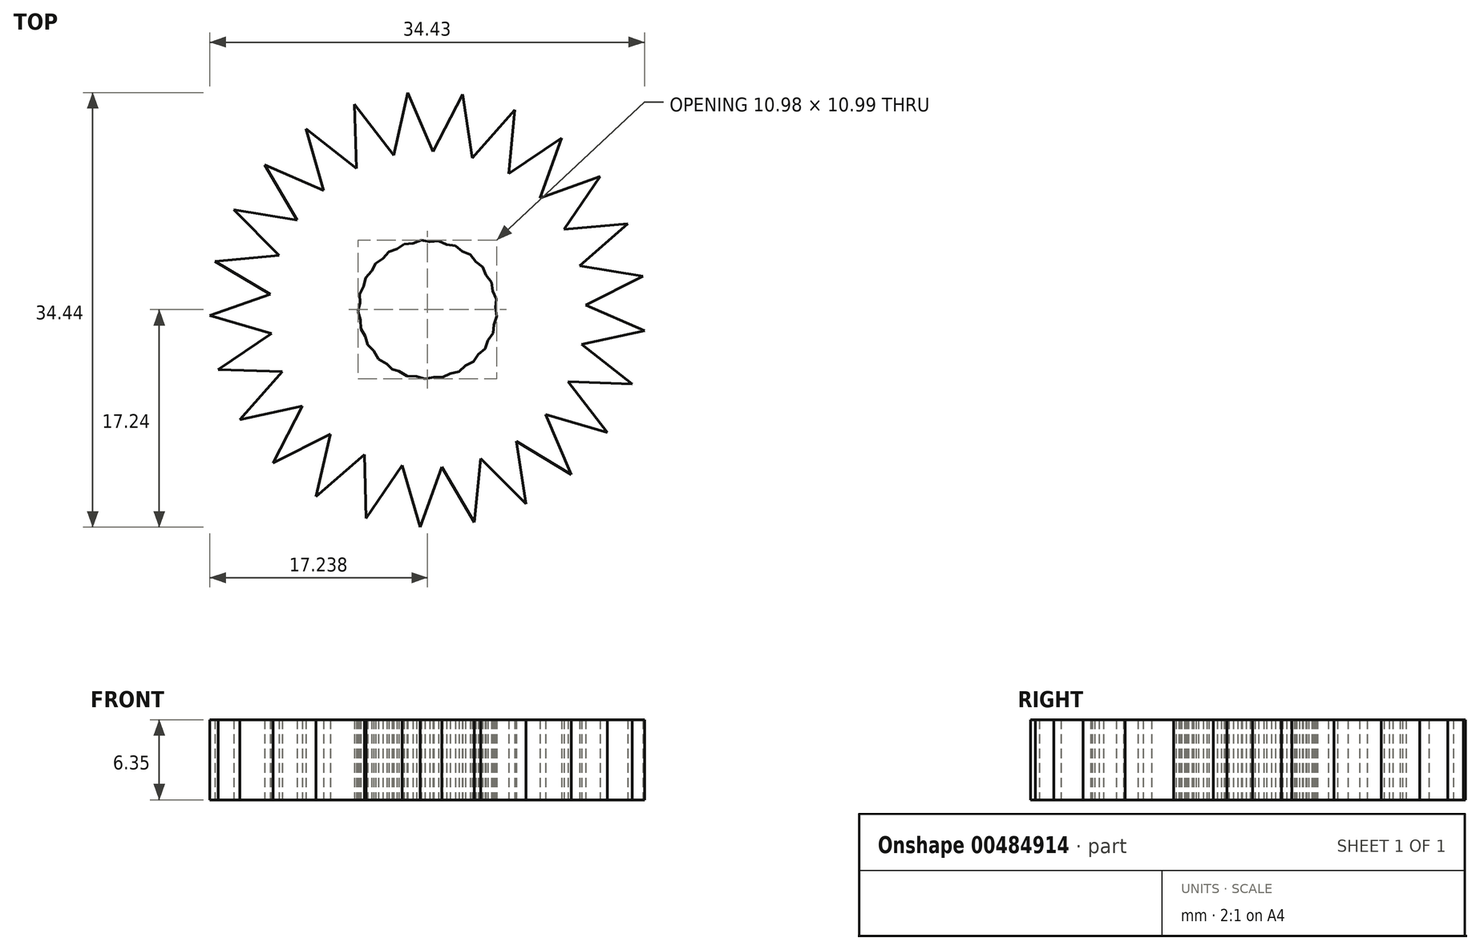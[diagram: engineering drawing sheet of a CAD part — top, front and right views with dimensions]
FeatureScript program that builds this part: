
annotation { "Feature Type Name" : "Feature", "Feature Type Description" : "" }
export const myFeature = defineFeature(function(context is Context, id is Id, definition is map)
    precondition{}
    {
        {
            var Q0;
            Q0=qCreatedBy(makeId("Top.planeOp"),FACE);
            var sketch = newSketch(context, id + "F0", { "sketchPlane" : qUnion([Q0])});
            skLineSegment(sketch, "E0", {"start": v(-12.25, -12.16) * mm, "end": v(2.76, 17.04) * mm});
            skLineSegment(sketch, "E1", {"start": v(2.76, 17.04) * mm, "end": v(7.78, -15.4) * mm});
            skLineSegment(sketch, "E2", {"start": v(7.78, -15.4) * mm, "end": v(-15.35, 7.9) * mm});
            skLineSegment(sketch, "E3", {"start": v(-15.35, 7.9) * mm, "end": v(17.06, 2.64) * mm});
            skLineSegment(sketch, "E4", {"start": v(17.06, 2.64) * mm, "end": v(-12.25, -12.16) * mm});
            skLineSegment(sketch, "E5", {"start": v(-14.89, -8.73) * mm, "end": v(6.91, 15.82) * mm});
            skLineSegment(sketch, "E6", {"start": v(6.91, 15.82) * mm, "end": v(3.7, -16.86) * mm});
            skLineSegment(sketch, "E7", {"start": v(3.7, -16.86) * mm, "end": v(-12.9, 11.46) * mm});
            skLineSegment(sketch, "E8", {"start": v(-12.9, 11.46) * mm, "end": v(17.18, -1.69) * mm});
            skLineSegment(sketch, "E9", {"start": v(17.18, -1.69) * mm, "end": v(-14.89, -8.73) * mm});
            skLineSegment(sketch, "E10", {"start": v(-16.6, -4.76) * mm, "end": v(10.63, 13.6) * mm});
            skLineSegment(sketch, "E11", {"start": v(10.63, 13.6) * mm, "end": v(-0.6, -17.25) * mm});
            skLineSegment(sketch, "E12", {"start": v(-0.6, -17.25) * mm, "end": v(-9.65, 14.3) * mm});
            skLineSegment(sketch, "E13", {"start": v(-9.65, 14.3) * mm, "end": v(16.22, -5.9) * mm});
            skLineSegment(sketch, "E14", {"start": v(16.22, -5.9) * mm, "end": v(-16.6, -4.76) * mm});
            skLineSegment(sketch, "E15", {"start": v(-17.25, -0.48) * mm, "end": v(13.68, 10.53) * mm});
            skLineSegment(sketch, "E16", {"start": v(-4.87, -16.56) * mm, "end": v(-5.79, 16.26) * mm});
            skLineSegment(sketch, "E17", {"start": v(-5.79, 16.26) * mm, "end": v(14.24, -9.75) * mm});
            skLineSegment(sketch, "E18", {"start": v(14.24, -9.75) * mm, "end": v(-17.25, -0.48) * mm});
            skLineSegment(sketch, "E19", {"start": v(-16.83, 3.82) * mm, "end": v(15.86, 6.8) * mm});
            skLineSegment(sketch, "E20", {"start": v(15.86, 6.8) * mm, "end": v(-8.84, -14.82) * mm});
            skLineSegment(sketch, "E21", {"start": v(-8.84, -14.82) * mm, "end": v(-1.56, 17.19) * mm});
            skLineSegment(sketch, "E22", {"start": v(11.4, -13.08) * mm, "end": v(-16.83, 3.82) * mm});
            skLineSegment(sketch, "E23", {"start": v(13.68, 10.53) * mm, "end": v(-4.87, -16.56) * mm});
            skLineSegment(sketch, "E24", {"start": v(-1.56, 17.19) * mm, "end": v(11.4, -13.08) * mm});
            skSolve(sketch);
        }
        {
            var Q0;
            {var subQ0=sQuery(id+"F0.wireOp",EDGE,"E4");var subQ1=sQuery(id+"F0.wireOp",EDGE,"E0");var subQ2=makeQuery(id+"F0.imprint","INTERSECT",VERTEX,{"derivedFrom":[subQ1,subQ0]});Q0=makeQuery(id+"F0.imprint","IMPRINT",FACE,{"disambiguationData":[TD([[makeQuery(id+"F0.imprint","IMPRINT",EDGE,{"disambiguationData":[TD([[subQ2,-1.0]])],"derivedFrom":subQ1}),-1.0]])]});}
            var Q1;
            {var subQ0=sQuery(id+"F0.wireOp",EDGE,"E9");var subQ1=sQuery(id+"F0.wireOp",EDGE,"E0");var subQ2=makeQuery(id+"F0.imprint","INTERSECT",VERTEX,{"derivedFrom":[subQ1,subQ0]});Q1=makeQuery(id+"F0.imprint","IMPRINT",FACE,{"disambiguationData":[TD([[makeQuery(id+"F0.imprint","IMPRINT",EDGE,{"disambiguationData":[TD([[subQ2,-1.0]])],"derivedFrom":subQ1}),1.0]])]});}
            var Q2;
            {var subQ0=sQuery(id+"F0.wireOp",EDGE,"E24");var subQ1=sQuery(id+"F0.wireOp",EDGE,"E0");var subQ2=makeQuery(id+"F0.imprint","INTERSECT",VERTEX,{"derivedFrom":[subQ1,subQ0]});Q2=makeQuery(id+"F0.imprint","IMPRINT",FACE,{"disambiguationData":[TD([[makeQuery(id+"F0.imprint","IMPRINT",EDGE,{"disambiguationData":[TD([[subQ2,1.0]])],"derivedFrom":subQ1}),1.0]])]});}
            var Q3;
            {var subQ0=sQuery(id+"F0.wireOp",EDGE,"E1");var subQ1=sQuery(id+"F0.wireOp",EDGE,"E0");var subQ2=makeQuery(id+"F0.imprint","INTERSECT",VERTEX,{"derivedFrom":[subQ1,subQ0]});Q3=makeQuery(id+"F0.imprint","IMPRINT",FACE,{"disambiguationData":[TD([[makeQuery(id+"F0.imprint","IMPRINT",EDGE,{"disambiguationData":[TD([[subQ2,1.0]])],"derivedFrom":subQ1}),-1.0]])]});}
            var Q4;
            {var subQ0=sQuery(id+"F0.wireOp",EDGE,"E5");var subQ1=sQuery(id+"F0.wireOp",EDGE,"E1");var subQ2=makeQuery(id+"F0.imprint","INTERSECT",VERTEX,{"derivedFrom":[subQ1,subQ0]});Q4=makeQuery(id+"F0.imprint","IMPRINT",FACE,{"disambiguationData":[TD([[makeQuery(id+"F0.imprint","IMPRINT",EDGE,{"disambiguationData":[TD([[subQ2,-1.0]])],"derivedFrom":subQ1}),1.0]])]});}
            var Q5;
            {var subQ0=sQuery(id+"F0.wireOp",EDGE,"E22");var subQ1=sQuery(id+"F0.wireOp",EDGE,"E1");var subQ2=makeQuery(id+"F0.imprint","INTERSECT",VERTEX,{"derivedFrom":[subQ1,subQ0]});Q5=makeQuery(id+"F0.imprint","IMPRINT",FACE,{"disambiguationData":[TD([[makeQuery(id+"F0.imprint","IMPRINT",EDGE,{"disambiguationData":[TD([[subQ2,1.0]])],"derivedFrom":subQ1}),1.0]])]});}
            var Q6;
            {var subQ0=sQuery(id+"F0.wireOp",EDGE,"E2");var subQ1=sQuery(id+"F0.wireOp",EDGE,"E1");var subQ2=makeQuery(id+"F0.imprint","INTERSECT",VERTEX,{"derivedFrom":[subQ1,subQ0]});Q6=makeQuery(id+"F0.imprint","IMPRINT",FACE,{"disambiguationData":[TD([[makeQuery(id+"F0.imprint","IMPRINT",EDGE,{"disambiguationData":[TD([[subQ2,1.0]])],"derivedFrom":subQ1}),-1.0]])]});}
            var Q7;
            {var subQ0=sQuery(id+"F0.wireOp",EDGE,"E6");var subQ1=sQuery(id+"F0.wireOp",EDGE,"E2");var subQ2=makeQuery(id+"F0.imprint","INTERSECT",VERTEX,{"derivedFrom":[subQ1,subQ0]});Q7=makeQuery(id+"F0.imprint","IMPRINT",FACE,{"disambiguationData":[TD([[makeQuery(id+"F0.imprint","IMPRINT",EDGE,{"disambiguationData":[TD([[subQ2,-1.0]])],"derivedFrom":subQ1}),1.0]])]});}
            var Q8;
            {var subQ0=sQuery(id+"F0.wireOp",EDGE,"E19");var subQ1=sQuery(id+"F0.wireOp",EDGE,"E2");var subQ2=makeQuery(id+"F0.imprint","INTERSECT",VERTEX,{"derivedFrom":[subQ1,subQ0]});Q8=makeQuery(id+"F0.imprint","IMPRINT",FACE,{"disambiguationData":[TD([[makeQuery(id+"F0.imprint","IMPRINT",EDGE,{"disambiguationData":[TD([[subQ2,1.0]])],"derivedFrom":subQ1}),1.0]])]});}
            var Q9;
            {var subQ0=sQuery(id+"F0.wireOp",EDGE,"E3");var subQ1=sQuery(id+"F0.wireOp",EDGE,"E2");var subQ2=makeQuery(id+"F0.imprint","INTERSECT",VERTEX,{"derivedFrom":[subQ1,subQ0]});Q9=makeQuery(id+"F0.imprint","IMPRINT",FACE,{"disambiguationData":[TD([[makeQuery(id+"F0.imprint","IMPRINT",EDGE,{"disambiguationData":[TD([[subQ2,1.0]])],"derivedFrom":subQ1}),-1.0]])]});}
            var Q10;
            {var subQ0=sQuery(id+"F0.wireOp",EDGE,"E7");var subQ1=sQuery(id+"F0.wireOp",EDGE,"E3");var subQ2=makeQuery(id+"F0.imprint","INTERSECT",VERTEX,{"derivedFrom":[subQ1,subQ0]});Q10=makeQuery(id+"F0.imprint","IMPRINT",FACE,{"disambiguationData":[TD([[makeQuery(id+"F0.imprint","IMPRINT",EDGE,{"disambiguationData":[TD([[subQ2,-1.0]])],"derivedFrom":subQ1}),1.0]])]});}
            var Q11;
            {var subQ0=sQuery(id+"F0.wireOp",EDGE,"E20");var subQ1=sQuery(id+"F0.wireOp",EDGE,"E3");var subQ2=makeQuery(id+"F0.imprint","INTERSECT",VERTEX,{"derivedFrom":[subQ1,subQ0]});Q11=makeQuery(id+"F0.imprint","IMPRINT",FACE,{"disambiguationData":[TD([[makeQuery(id+"F0.imprint","IMPRINT",EDGE,{"disambiguationData":[TD([[subQ2,1.0]])],"derivedFrom":subQ1}),1.0]])]});}
            var Q12;
            {var subQ0=sQuery(id+"F0.wireOp",EDGE,"E4");var subQ1=sQuery(id+"F0.wireOp",EDGE,"E3");var subQ2=makeQuery(id+"F0.imprint","INTERSECT",VERTEX,{"derivedFrom":[subQ1,subQ0]});Q12=makeQuery(id+"F0.imprint","IMPRINT",FACE,{"disambiguationData":[TD([[makeQuery(id+"F0.imprint","IMPRINT",EDGE,{"disambiguationData":[TD([[subQ2,1.0]])],"derivedFrom":subQ1}),-1.0]])]});}
            var Q13;
            {var subQ0=sQuery(id+"F0.wireOp",EDGE,"E8");var subQ1=sQuery(id+"F0.wireOp",EDGE,"E4");var subQ2=makeQuery(id+"F0.imprint","INTERSECT",VERTEX,{"derivedFrom":[subQ1,subQ0]});Q13=makeQuery(id+"F0.imprint","IMPRINT",FACE,{"disambiguationData":[TD([[makeQuery(id+"F0.imprint","IMPRINT",EDGE,{"disambiguationData":[TD([[subQ2,-1.0]])],"derivedFrom":subQ1}),1.0]])]});}
            var Q14;
            {var subQ0=sQuery(id+"F0.wireOp",EDGE,"E21");var subQ1=sQuery(id+"F0.wireOp",EDGE,"E4");var subQ2=makeQuery(id+"F0.imprint","INTERSECT",VERTEX,{"derivedFrom":[subQ1,subQ0]});Q14=makeQuery(id+"F0.imprint","IMPRINT",FACE,{"disambiguationData":[TD([[makeQuery(id+"F0.imprint","IMPRINT",EDGE,{"disambiguationData":[TD([[subQ2,1.0]])],"derivedFrom":subQ1}),1.0]])]});}
            var Q15;
            {var subQ0=sQuery(id+"F0.wireOp",EDGE,"E14");var subQ1=sQuery(id+"F0.wireOp",EDGE,"E5");var subQ2=makeQuery(id+"F0.imprint","INTERSECT",VERTEX,{"derivedFrom":[subQ1,subQ0]});Q15=makeQuery(id+"F0.imprint","IMPRINT",FACE,{"disambiguationData":[TD([[makeQuery(id+"F0.imprint","IMPRINT",EDGE,{"disambiguationData":[TD([[subQ2,-1.0]])],"derivedFrom":subQ1}),1.0]])]});}
            var Q16;
            {var subQ0=sQuery(id+"F0.wireOp",EDGE,"E10");var subQ1=sQuery(id+"F0.wireOp",EDGE,"E6");var subQ2=makeQuery(id+"F0.imprint","INTERSECT",VERTEX,{"derivedFrom":[subQ1,subQ0]});Q16=makeQuery(id+"F0.imprint","IMPRINT",FACE,{"disambiguationData":[TD([[makeQuery(id+"F0.imprint","IMPRINT",EDGE,{"disambiguationData":[TD([[subQ2,-1.0]])],"derivedFrom":subQ1}),1.0]])]});}
            var Q17;
            {var subQ0=sQuery(id+"F0.wireOp",EDGE,"E11");var subQ1=sQuery(id+"F0.wireOp",EDGE,"E7");var subQ2=makeQuery(id+"F0.imprint","INTERSECT",VERTEX,{"derivedFrom":[subQ1,subQ0]});Q17=makeQuery(id+"F0.imprint","IMPRINT",FACE,{"disambiguationData":[TD([[makeQuery(id+"F0.imprint","IMPRINT",EDGE,{"disambiguationData":[TD([[subQ2,-1.0]])],"derivedFrom":subQ1}),1.0]])]});}
            var Q18;
            {var subQ0=sQuery(id+"F0.wireOp",EDGE,"E12");var subQ1=sQuery(id+"F0.wireOp",EDGE,"E8");var subQ2=makeQuery(id+"F0.imprint","INTERSECT",VERTEX,{"derivedFrom":[subQ1,subQ0]});Q18=makeQuery(id+"F0.imprint","IMPRINT",FACE,{"disambiguationData":[TD([[makeQuery(id+"F0.imprint","IMPRINT",EDGE,{"disambiguationData":[TD([[subQ2,-1.0]])],"derivedFrom":subQ1}),1.0]])]});}
            var Q19;
            {var subQ0=sQuery(id+"F0.wireOp",EDGE,"E13");var subQ1=sQuery(id+"F0.wireOp",EDGE,"E9");var subQ2=makeQuery(id+"F0.imprint","INTERSECT",VERTEX,{"derivedFrom":[subQ1,subQ0]});Q19=makeQuery(id+"F0.imprint","IMPRINT",FACE,{"disambiguationData":[TD([[makeQuery(id+"F0.imprint","IMPRINT",EDGE,{"disambiguationData":[TD([[subQ2,-1.0]])],"derivedFrom":subQ1}),1.0]])]});}
            var Q20;
            {var subQ0=sQuery(id+"F0.wireOp",EDGE,"E18");var subQ1=sQuery(id+"F0.wireOp",EDGE,"E10");var subQ2=makeQuery(id+"F0.imprint","INTERSECT",VERTEX,{"derivedFrom":[subQ1,subQ0]});Q20=makeQuery(id+"F0.imprint","IMPRINT",FACE,{"disambiguationData":[TD([[makeQuery(id+"F0.imprint","IMPRINT",EDGE,{"disambiguationData":[TD([[subQ2,-1.0]])],"derivedFrom":subQ1}),1.0]])]});}
            var Q21;
            {var subQ0=sQuery(id+"F0.wireOp",EDGE,"E15");var subQ1=sQuery(id+"F0.wireOp",EDGE,"E11");var subQ2=makeQuery(id+"F0.imprint","INTERSECT",VERTEX,{"derivedFrom":[subQ1,subQ0]});Q21=makeQuery(id+"F0.imprint","IMPRINT",FACE,{"disambiguationData":[TD([[makeQuery(id+"F0.imprint","IMPRINT",EDGE,{"disambiguationData":[TD([[subQ2,-1.0]])],"derivedFrom":subQ1}),1.0]])]});}
            var Q22;
            {var subQ0=sQuery(id+"F0.wireOp",EDGE,"E23");var subQ1=sQuery(id+"F0.wireOp",EDGE,"E12");var subQ2=makeQuery(id+"F0.imprint","INTERSECT",VERTEX,{"derivedFrom":[subQ1,subQ0]});Q22=makeQuery(id+"F0.imprint","IMPRINT",FACE,{"disambiguationData":[TD([[makeQuery(id+"F0.imprint","IMPRINT",EDGE,{"disambiguationData":[TD([[subQ2,-1.0]])],"derivedFrom":subQ1}),1.0]])]});}
            var Q23;
            {var subQ0=sQuery(id+"F0.wireOp",EDGE,"E16");var subQ1=sQuery(id+"F0.wireOp",EDGE,"E13");var subQ2=makeQuery(id+"F0.imprint","INTERSECT",VERTEX,{"derivedFrom":[subQ1,subQ0]});Q23=makeQuery(id+"F0.imprint","IMPRINT",FACE,{"disambiguationData":[TD([[makeQuery(id+"F0.imprint","IMPRINT",EDGE,{"disambiguationData":[TD([[subQ2,-1.0]])],"derivedFrom":subQ1}),1.0]])]});}
            var Q24;
            {var subQ0=sQuery(id+"F0.wireOp",EDGE,"E17");var subQ1=sQuery(id+"F0.wireOp",EDGE,"E14");var subQ2=makeQuery(id+"F0.imprint","INTERSECT",VERTEX,{"derivedFrom":[subQ1,subQ0]});Q24=makeQuery(id+"F0.imprint","IMPRINT",FACE,{"disambiguationData":[TD([[makeQuery(id+"F0.imprint","IMPRINT",EDGE,{"disambiguationData":[TD([[subQ2,-1.0]])],"derivedFrom":subQ1}),1.0]])]});}
            var Q25;
            {var subQ0=sQuery(id+"F0.wireOp",EDGE,"E14");var subQ1=sQuery(id+"F0.wireOp",EDGE,"E0");var subQ2=makeQuery(id+"F0.imprint","INTERSECT",VERTEX,{"derivedFrom":[subQ1,subQ0]});Q25=makeQuery(id+"F0.imprint","IMPRINT",FACE,{"disambiguationData":[TD([[makeQuery(id+"F0.imprint","IMPRINT",EDGE,{"disambiguationData":[TD([[subQ2,-1.0]])],"derivedFrom":subQ1}),1.0]])]});}
            var Q26;
            {var subQ0=sQuery(id+"F0.wireOp",EDGE,"E24");var subQ1=sQuery(id+"F0.wireOp",EDGE,"E0");var subQ2=makeQuery(id+"F0.imprint","INTERSECT",VERTEX,{"derivedFrom":[subQ1,subQ0]});Q26=makeQuery(id+"F0.imprint","IMPRINT",FACE,{"disambiguationData":[TD([[makeQuery(id+"F0.imprint","IMPRINT",EDGE,{"disambiguationData":[TD([[subQ2,1.0]])],"derivedFrom":subQ1}),-1.0]])]});}
            var Q27;
            {var subQ0=sQuery(id+"F0.wireOp",EDGE,"E10");var subQ1=sQuery(id+"F0.wireOp",EDGE,"E1");var subQ2=makeQuery(id+"F0.imprint","INTERSECT",VERTEX,{"derivedFrom":[subQ1,subQ0]});Q27=makeQuery(id+"F0.imprint","IMPRINT",FACE,{"disambiguationData":[TD([[makeQuery(id+"F0.imprint","IMPRINT",EDGE,{"disambiguationData":[TD([[subQ2,-1.0]])],"derivedFrom":subQ1}),1.0]])]});}
            var Q28;
            {var subQ0=sQuery(id+"F0.wireOp",EDGE,"E14");var subQ1=sQuery(id+"F0.wireOp",EDGE,"E1");var subQ2=makeQuery(id+"F0.imprint","INTERSECT",VERTEX,{"derivedFrom":[subQ1,subQ0]});Q28=makeQuery(id+"F0.imprint","IMPRINT",FACE,{"disambiguationData":[TD([[makeQuery(id+"F0.imprint","IMPRINT",EDGE,{"disambiguationData":[TD([[subQ2,-1.0]])],"derivedFrom":subQ1}),1.0]])]});}
            var Q29;
            {var subQ0=sQuery(id+"F0.wireOp",EDGE,"E6");var subQ1=sQuery(id+"F0.wireOp",EDGE,"E2");var subQ2=makeQuery(id+"F0.imprint","INTERSECT",VERTEX,{"derivedFrom":[subQ1,subQ0]});Q29=makeQuery(id+"F0.imprint","IMPRINT",FACE,{"disambiguationData":[TD([[makeQuery(id+"F0.imprint","IMPRINT",EDGE,{"disambiguationData":[TD([[subQ2,-1.0]])],"derivedFrom":subQ1}),-1.0]])]});}
            var Q30;
            {var subQ0=sQuery(id+"F0.wireOp",EDGE,"E11");var subQ1=sQuery(id+"F0.wireOp",EDGE,"E2");var subQ2=makeQuery(id+"F0.imprint","INTERSECT",VERTEX,{"derivedFrom":[subQ1,subQ0]});Q30=makeQuery(id+"F0.imprint","IMPRINT",FACE,{"disambiguationData":[TD([[makeQuery(id+"F0.imprint","IMPRINT",EDGE,{"disambiguationData":[TD([[subQ2,-1.0]])],"derivedFrom":subQ1}),1.0]])]});}
            var Q31;
            {var subQ0=sQuery(id+"F0.wireOp",EDGE,"E10");var subQ1=sQuery(id+"F0.wireOp",EDGE,"E2");var subQ2=makeQuery(id+"F0.imprint","INTERSECT",VERTEX,{"derivedFrom":[subQ1,subQ0]});Q31=makeQuery(id+"F0.imprint","IMPRINT",FACE,{"disambiguationData":[TD([[makeQuery(id+"F0.imprint","IMPRINT",EDGE,{"disambiguationData":[TD([[subQ2,-1.0]])],"derivedFrom":subQ1}),1.0]])]});}
            var Q32;
            {var subQ0=sQuery(id+"F0.wireOp",EDGE,"E7");var subQ1=sQuery(id+"F0.wireOp",EDGE,"E3");var subQ2=makeQuery(id+"F0.imprint","INTERSECT",VERTEX,{"derivedFrom":[subQ1,subQ0]});Q32=makeQuery(id+"F0.imprint","IMPRINT",FACE,{"disambiguationData":[TD([[makeQuery(id+"F0.imprint","IMPRINT",EDGE,{"disambiguationData":[TD([[subQ2,-1.0]])],"derivedFrom":subQ1}),-1.0]])]});}
            var Q33;
            {var subQ0=sQuery(id+"F0.wireOp",EDGE,"E12");var subQ1=sQuery(id+"F0.wireOp",EDGE,"E3");var subQ2=makeQuery(id+"F0.imprint","INTERSECT",VERTEX,{"derivedFrom":[subQ1,subQ0]});Q33=makeQuery(id+"F0.imprint","IMPRINT",FACE,{"disambiguationData":[TD([[makeQuery(id+"F0.imprint","IMPRINT",EDGE,{"disambiguationData":[TD([[subQ2,-1.0]])],"derivedFrom":subQ1}),1.0]])]});}
            var Q34;
            {var subQ0=sQuery(id+"F0.wireOp",EDGE,"E20");var subQ1=sQuery(id+"F0.wireOp",EDGE,"E3");var subQ2=makeQuery(id+"F0.imprint","INTERSECT",VERTEX,{"derivedFrom":[subQ1,subQ0]});Q34=makeQuery(id+"F0.imprint","IMPRINT",FACE,{"disambiguationData":[TD([[makeQuery(id+"F0.imprint","IMPRINT",EDGE,{"disambiguationData":[TD([[subQ2,1.0]])],"derivedFrom":subQ1}),-1.0]])]});}
            var Q35;
            {var subQ0=sQuery(id+"F0.wireOp",EDGE,"E8");var subQ1=sQuery(id+"F0.wireOp",EDGE,"E4");var subQ2=makeQuery(id+"F0.imprint","INTERSECT",VERTEX,{"derivedFrom":[subQ1,subQ0]});Q35=makeQuery(id+"F0.imprint","IMPRINT",FACE,{"disambiguationData":[TD([[makeQuery(id+"F0.imprint","IMPRINT",EDGE,{"disambiguationData":[TD([[subQ2,-1.0]])],"derivedFrom":subQ1}),-1.0]])]});}
            var Q36;
            {var subQ0=sQuery(id+"F0.wireOp",EDGE,"E12");var subQ1=sQuery(id+"F0.wireOp",EDGE,"E4");var subQ2=makeQuery(id+"F0.imprint","INTERSECT",VERTEX,{"derivedFrom":[subQ1,subQ0]});Q36=makeQuery(id+"F0.imprint","IMPRINT",FACE,{"disambiguationData":[TD([[makeQuery(id+"F0.imprint","IMPRINT",EDGE,{"disambiguationData":[TD([[subQ2,-1.0]])],"derivedFrom":subQ1}),1.0]])]});}
            var Q37;
            {var subQ0=sQuery(id+"F0.wireOp",EDGE,"E21");var subQ1=sQuery(id+"F0.wireOp",EDGE,"E4");var subQ2=makeQuery(id+"F0.imprint","INTERSECT",VERTEX,{"derivedFrom":[subQ1,subQ0]});Q37=makeQuery(id+"F0.imprint","IMPRINT",FACE,{"disambiguationData":[TD([[makeQuery(id+"F0.imprint","IMPRINT",EDGE,{"disambiguationData":[TD([[subQ2,1.0]])],"derivedFrom":subQ1}),-1.0]])]});}
            var Q38;
            {var subQ0=sQuery(id+"F0.wireOp",EDGE,"E18");var subQ1=sQuery(id+"F0.wireOp",EDGE,"E5");var subQ2=makeQuery(id+"F0.imprint","INTERSECT",VERTEX,{"derivedFrom":[subQ1,subQ0]});Q38=makeQuery(id+"F0.imprint","IMPRINT",FACE,{"disambiguationData":[TD([[makeQuery(id+"F0.imprint","IMPRINT",EDGE,{"disambiguationData":[TD([[subQ2,-1.0]])],"derivedFrom":subQ1}),1.0]])]});}
            var Q39;
            {var subQ0=sQuery(id+"F0.wireOp",EDGE,"E15");var subQ1=sQuery(id+"F0.wireOp",EDGE,"E6");var subQ2=makeQuery(id+"F0.imprint","INTERSECT",VERTEX,{"derivedFrom":[subQ1,subQ0]});Q39=makeQuery(id+"F0.imprint","IMPRINT",FACE,{"disambiguationData":[TD([[makeQuery(id+"F0.imprint","IMPRINT",EDGE,{"disambiguationData":[TD([[subQ2,-1.0]])],"derivedFrom":subQ1}),1.0]])]});}
            var Q40;
            {var subQ0=sQuery(id+"F0.wireOp",EDGE,"E17");var subQ1=sQuery(id+"F0.wireOp",EDGE,"E9");var subQ2=makeQuery(id+"F0.imprint","INTERSECT",VERTEX,{"derivedFrom":[subQ1,subQ0]});Q40=makeQuery(id+"F0.imprint","IMPRINT",FACE,{"disambiguationData":[TD([[makeQuery(id+"F0.imprint","IMPRINT",EDGE,{"disambiguationData":[TD([[subQ2,-1.0]])],"derivedFrom":subQ1}),1.0]])]});}
            var Q41;
            {var subQ0=sQuery(id+"F0.wireOp",EDGE,"E7");var subQ1=sQuery(id+"F0.wireOp",EDGE,"E4");var subQ2=makeQuery(id+"F0.imprint","INTERSECT",VERTEX,{"derivedFrom":[subQ1,subQ0]});Q41=makeQuery(id+"F0.imprint","IMPRINT",FACE,{"disambiguationData":[TD([[makeQuery(id+"F0.imprint","IMPRINT",EDGE,{"disambiguationData":[TD([[subQ2,-1.0]])],"derivedFrom":subQ1}),1.0]])]});}
            var Q42;
            {var subQ0=sQuery(id+"F0.wireOp",EDGE,"E16");var subQ1=sQuery(id+"F0.wireOp",EDGE,"E9");var subQ2=makeQuery(id+"F0.imprint","INTERSECT",VERTEX,{"derivedFrom":[subQ1,subQ0]});Q42=makeQuery(id+"F0.imprint","IMPRINT",FACE,{"disambiguationData":[TD([[makeQuery(id+"F0.imprint","IMPRINT",EDGE,{"disambiguationData":[TD([[subQ2,-1.0]])],"derivedFrom":subQ1}),-1.0]])]});}
            var Q43;
            {var subQ0=sQuery(id+"F0.wireOp",EDGE,"E18");var subQ1=sQuery(id+"F0.wireOp",EDGE,"E0");var subQ2=makeQuery(id+"F0.imprint","INTERSECT",VERTEX,{"derivedFrom":[subQ1,subQ0]});Q43=makeQuery(id+"F0.imprint","IMPRINT",FACE,{"disambiguationData":[TD([[makeQuery(id+"F0.imprint","IMPRINT",EDGE,{"disambiguationData":[TD([[subQ2,-1.0]])],"derivedFrom":subQ1}),1.0]])]});}
            var Q44;
            {var subQ0=sQuery(id+"F0.wireOp",EDGE,"E10");var subQ1=sQuery(id+"F0.wireOp",EDGE,"E2");var subQ2=makeQuery(id+"F0.imprint","INTERSECT",VERTEX,{"derivedFrom":[subQ1,subQ0]});Q44=makeQuery(id+"F0.imprint","IMPRINT",FACE,{"disambiguationData":[TD([[makeQuery(id+"F0.imprint","IMPRINT",EDGE,{"disambiguationData":[TD([[subQ2,-1.0]])],"derivedFrom":subQ1}),-1.0]])]});}
            var Q45;
            {var subQ0=sQuery(id+"F0.wireOp",EDGE,"E12");var subQ1=sQuery(id+"F0.wireOp",EDGE,"E3");var subQ2=makeQuery(id+"F0.imprint","INTERSECT",VERTEX,{"derivedFrom":[subQ1,subQ0]});Q45=makeQuery(id+"F0.imprint","IMPRINT",FACE,{"disambiguationData":[TD([[makeQuery(id+"F0.imprint","IMPRINT",EDGE,{"disambiguationData":[TD([[subQ2,-1.0]])],"derivedFrom":subQ1}),-1.0]])]});}
            var Q46;
            {var subQ0=sQuery(id+"F0.wireOp",EDGE,"E8");var subQ1=sQuery(id+"F0.wireOp",EDGE,"E0");var subQ2=makeQuery(id+"F0.imprint","INTERSECT",VERTEX,{"derivedFrom":[subQ1,subQ0]});Q46=makeQuery(id+"F0.imprint","IMPRINT",FACE,{"disambiguationData":[TD([[makeQuery(id+"F0.imprint","IMPRINT",EDGE,{"disambiguationData":[TD([[subQ2,-1.0]])],"derivedFrom":subQ1}),1.0]])]});}
            var Q47;
            {var subQ0=sQuery(id+"F0.wireOp",EDGE,"E17");var subQ1=sQuery(id+"F0.wireOp",EDGE,"E5");var subQ2=makeQuery(id+"F0.imprint","INTERSECT",VERTEX,{"derivedFrom":[subQ1,subQ0]});Q47=makeQuery(id+"F0.imprint","IMPRINT",FACE,{"disambiguationData":[TD([[makeQuery(id+"F0.imprint","IMPRINT",EDGE,{"disambiguationData":[TD([[subQ2,-1.0]])],"derivedFrom":subQ1}),-1.0]])]});}
            var Q48;
            {var subQ0=sQuery(id+"F0.wireOp",EDGE,"E15");var subQ1=sQuery(id+"F0.wireOp",EDGE,"E1");var subQ2=makeQuery(id+"F0.imprint","INTERSECT",VERTEX,{"derivedFrom":[subQ1,subQ0]});Q48=makeQuery(id+"F0.imprint","IMPRINT",FACE,{"disambiguationData":[TD([[makeQuery(id+"F0.imprint","IMPRINT",EDGE,{"disambiguationData":[TD([[subQ2,-1.0]])],"derivedFrom":subQ1}),1.0]])]});}
            var Q49;
            {var subQ0=sQuery(id+"F0.wireOp",EDGE,"E11");var subQ1=sQuery(id+"F0.wireOp",EDGE,"E3");var subQ2=makeQuery(id+"F0.imprint","INTERSECT",VERTEX,{"derivedFrom":[subQ1,subQ0]});Q49=makeQuery(id+"F0.imprint","IMPRINT",FACE,{"disambiguationData":[TD([[makeQuery(id+"F0.imprint","IMPRINT",EDGE,{"disambiguationData":[TD([[subQ2,-1.0]])],"derivedFrom":subQ1}),-1.0]])]});}
            var Q50;
            {var subQ0=sQuery(id+"F0.wireOp",EDGE,"E13");var subQ1=sQuery(id+"F0.wireOp",EDGE,"E4");var subQ2=makeQuery(id+"F0.imprint","INTERSECT",VERTEX,{"derivedFrom":[subQ1,subQ0]});Q50=makeQuery(id+"F0.imprint","IMPRINT",FACE,{"disambiguationData":[TD([[makeQuery(id+"F0.imprint","IMPRINT",EDGE,{"disambiguationData":[TD([[subQ2,-1.0]])],"derivedFrom":subQ1}),-1.0]])]});}
            var Q51;
            {var subQ0=sQuery(id+"F0.wireOp",EDGE,"E9");var subQ1=sQuery(id+"F0.wireOp",EDGE,"E1");var subQ2=makeQuery(id+"F0.imprint","INTERSECT",VERTEX,{"derivedFrom":[subQ1,subQ0]});Q51=makeQuery(id+"F0.imprint","IMPRINT",FACE,{"disambiguationData":[TD([[makeQuery(id+"F0.imprint","IMPRINT",EDGE,{"disambiguationData":[TD([[subQ2,-1.0]])],"derivedFrom":subQ1}),1.0]])]});}
            var Q52;
            {var subQ0=sQuery(id+"F0.wireOp",EDGE,"E18");var subQ1=sQuery(id+"F0.wireOp",EDGE,"E6");var subQ2=makeQuery(id+"F0.imprint","INTERSECT",VERTEX,{"derivedFrom":[subQ1,subQ0]});Q52=makeQuery(id+"F0.imprint","IMPRINT",FACE,{"disambiguationData":[TD([[makeQuery(id+"F0.imprint","IMPRINT",EDGE,{"disambiguationData":[TD([[subQ2,-1.0]])],"derivedFrom":subQ1}),-1.0]])]});}
            var Q53;
            {var subQ0=sQuery(id+"F0.wireOp",EDGE,"E23");var subQ1=sQuery(id+"F0.wireOp",EDGE,"E2");var subQ2=makeQuery(id+"F0.imprint","INTERSECT",VERTEX,{"derivedFrom":[subQ1,subQ0]});Q53=makeQuery(id+"F0.imprint","IMPRINT",FACE,{"disambiguationData":[TD([[makeQuery(id+"F0.imprint","IMPRINT",EDGE,{"disambiguationData":[TD([[subQ2,-1.0]])],"derivedFrom":subQ1}),1.0]])]});}
            var Q54;
            {var subQ0=sQuery(id+"F0.wireOp",EDGE,"E11");var subQ1=sQuery(id+"F0.wireOp",EDGE,"E2");var subQ2=makeQuery(id+"F0.imprint","INTERSECT",VERTEX,{"derivedFrom":[subQ1,subQ0]});Q54=makeQuery(id+"F0.imprint","IMPRINT",FACE,{"disambiguationData":[TD([[makeQuery(id+"F0.imprint","IMPRINT",EDGE,{"disambiguationData":[TD([[subQ2,-1.0]])],"derivedFrom":subQ1}),-1.0]])]});}
            var Q55;
            {var subQ0=sQuery(id+"F0.wireOp",EDGE,"E14");var subQ1=sQuery(id+"F0.wireOp",EDGE,"E1");var subQ2=makeQuery(id+"F0.imprint","INTERSECT",VERTEX,{"derivedFrom":[subQ1,subQ0]});Q55=makeQuery(id+"F0.imprint","IMPRINT",FACE,{"disambiguationData":[TD([[makeQuery(id+"F0.imprint","IMPRINT",EDGE,{"disambiguationData":[TD([[subQ2,-1.0]])],"derivedFrom":subQ1}),-1.0]])]});}
            var Q56;
            {var subQ0=sQuery(id+"F0.wireOp",EDGE,"E17");var subQ1=sQuery(id+"F0.wireOp",EDGE,"E4");var subQ2=makeQuery(id+"F0.imprint","INTERSECT",VERTEX,{"derivedFrom":[subQ1,subQ0]});Q56=makeQuery(id+"F0.imprint","IMPRINT",FACE,{"disambiguationData":[TD([[makeQuery(id+"F0.imprint","IMPRINT",EDGE,{"disambiguationData":[TD([[subQ2,-1.0]])],"derivedFrom":subQ1}),1.0]])]});}
            var Q57;
            {var subQ0=sQuery(id+"F0.wireOp",EDGE,"E23");var subQ1=sQuery(id+"F0.wireOp",EDGE,"E8");var subQ2=makeQuery(id+"F0.imprint","INTERSECT",VERTEX,{"derivedFrom":[subQ1,subQ0]});Q57=makeQuery(id+"F0.imprint","IMPRINT",FACE,{"disambiguationData":[TD([[makeQuery(id+"F0.imprint","IMPRINT",EDGE,{"disambiguationData":[TD([[subQ2,-1.0]])],"derivedFrom":subQ1}),-1.0]])]});}
            var Q58;
            {var subQ0=sQuery(id+"F0.wireOp",EDGE,"E6");var subQ1=sQuery(id+"F0.wireOp",EDGE,"E3");var subQ2=makeQuery(id+"F0.imprint","INTERSECT",VERTEX,{"derivedFrom":[subQ1,subQ0]});Q58=makeQuery(id+"F0.imprint","IMPRINT",FACE,{"disambiguationData":[TD([[makeQuery(id+"F0.imprint","IMPRINT",EDGE,{"disambiguationData":[TD([[subQ2,-1.0]])],"derivedFrom":subQ1}),1.0]])]});}
            var Q59;
            {var subQ0=sQuery(id+"F0.wireOp",EDGE,"E10");var subQ1=sQuery(id+"F0.wireOp",EDGE,"E1");var subQ2=makeQuery(id+"F0.imprint","INTERSECT",VERTEX,{"derivedFrom":[subQ1,subQ0]});Q59=makeQuery(id+"F0.imprint","IMPRINT",FACE,{"disambiguationData":[TD([[makeQuery(id+"F0.imprint","IMPRINT",EDGE,{"disambiguationData":[TD([[subQ2,-1.0]])],"derivedFrom":subQ1}),-1.0]])]});}
            var Q60;
            {var subQ0=sQuery(id+"F0.wireOp",EDGE,"E13");var subQ1=sQuery(id+"F0.wireOp",EDGE,"E0");var subQ2=makeQuery(id+"F0.imprint","INTERSECT",VERTEX,{"derivedFrom":[subQ1,subQ0]});Q60=makeQuery(id+"F0.imprint","IMPRINT",FACE,{"disambiguationData":[TD([[makeQuery(id+"F0.imprint","IMPRINT",EDGE,{"disambiguationData":[TD([[subQ2,-1.0]])],"derivedFrom":subQ1}),-1.0]])]});}
            var Q61;
            {var subQ0=sQuery(id+"F0.wireOp",EDGE,"E16");var subQ1=sQuery(id+"F0.wireOp",EDGE,"E3");var subQ2=makeQuery(id+"F0.imprint","INTERSECT",VERTEX,{"derivedFrom":[subQ1,subQ0]});Q61=makeQuery(id+"F0.imprint","IMPRINT",FACE,{"disambiguationData":[TD([[makeQuery(id+"F0.imprint","IMPRINT",EDGE,{"disambiguationData":[TD([[subQ2,-1.0]])],"derivedFrom":subQ1}),1.0]])]});}
            var Q62;
            {var subQ0=sQuery(id+"F0.wireOp",EDGE,"E15");var subQ1=sQuery(id+"F0.wireOp",EDGE,"E7");var subQ2=makeQuery(id+"F0.imprint","INTERSECT",VERTEX,{"derivedFrom":[subQ1,subQ0]});Q62=makeQuery(id+"F0.imprint","IMPRINT",FACE,{"disambiguationData":[TD([[makeQuery(id+"F0.imprint","IMPRINT",EDGE,{"disambiguationData":[TD([[subQ2,-1.0]])],"derivedFrom":subQ1}),-1.0]])]});}
            var Q63;
            {var subQ0=sQuery(id+"F0.wireOp",EDGE,"E5");var subQ1=sQuery(id+"F0.wireOp",EDGE,"E2");var subQ2=makeQuery(id+"F0.imprint","INTERSECT",VERTEX,{"derivedFrom":[subQ1,subQ0]});Q63=makeQuery(id+"F0.imprint","IMPRINT",FACE,{"disambiguationData":[TD([[makeQuery(id+"F0.imprint","IMPRINT",EDGE,{"disambiguationData":[TD([[subQ2,-1.0]])],"derivedFrom":subQ1}),1.0]])]});}
            var Q64;
            {var subQ0=sQuery(id+"F0.wireOp",EDGE,"E14");var subQ1=sQuery(id+"F0.wireOp",EDGE,"E0");var subQ2=makeQuery(id+"F0.imprint","INTERSECT",VERTEX,{"derivedFrom":[subQ1,subQ0]});Q64=makeQuery(id+"F0.imprint","IMPRINT",FACE,{"disambiguationData":[TD([[makeQuery(id+"F0.imprint","IMPRINT",EDGE,{"disambiguationData":[TD([[subQ2,-1.0]])],"derivedFrom":subQ1}),-1.0]])]});}
            var Q65;
            {var subQ0=sQuery(id+"F0.wireOp",EDGE,"E12");var subQ1=sQuery(id+"F0.wireOp",EDGE,"E4");var subQ2=makeQuery(id+"F0.imprint","INTERSECT",VERTEX,{"derivedFrom":[subQ1,subQ0]});Q65=makeQuery(id+"F0.imprint","IMPRINT",FACE,{"disambiguationData":[TD([[makeQuery(id+"F0.imprint","IMPRINT",EDGE,{"disambiguationData":[TD([[subQ2,-1.0]])],"derivedFrom":subQ1}),-1.0]])]});}
            var Q66;
            {var subQ0=sQuery(id+"F0.wireOp",EDGE,"E16");var subQ1=sQuery(id+"F0.wireOp",EDGE,"E14");var subQ2=makeQuery(id+"F0.imprint","INTERSECT",VERTEX,{"derivedFrom":[subQ1,subQ0]});Q66=makeQuery(id+"F0.imprint","IMPRINT",FACE,{"disambiguationData":[TD([[makeQuery(id+"F0.imprint","IMPRINT",EDGE,{"disambiguationData":[TD([[subQ2,-1.0]])],"derivedFrom":subQ1}),-1.0]])]});}
            var Q67;
            {var subQ0=sQuery(id+"F0.wireOp",EDGE,"E22");var subQ1=sQuery(id+"F0.wireOp",EDGE,"E0");var subQ2=makeQuery(id+"F0.imprint","INTERSECT",VERTEX,{"derivedFrom":[subQ1,subQ0]});Q67=makeQuery(id+"F0.imprint","IMPRINT",FACE,{"disambiguationData":[TD([[makeQuery(id+"F0.imprint","IMPRINT",EDGE,{"disambiguationData":[TD([[subQ2,-1.0]])],"derivedFrom":subQ1}),1.0]])]});}
            var Q68;
            {var subQ0=sQuery(id+"F0.wireOp",EDGE,"E10");var subQ1=sQuery(id+"F0.wireOp",EDGE,"E7");var subQ2=makeQuery(id+"F0.imprint","INTERSECT",VERTEX,{"derivedFrom":[subQ1,subQ0]});Q68=makeQuery(id+"F0.imprint","IMPRINT",FACE,{"disambiguationData":[TD([[makeQuery(id+"F0.imprint","IMPRINT",EDGE,{"disambiguationData":[TD([[subQ2,-1.0]])],"derivedFrom":subQ1}),-1.0]])]});}
            var Q69;
            {var subQ0=sQuery(id+"F0.wireOp",EDGE,"E16");var subQ1=sQuery(id+"F0.wireOp",EDGE,"E3");var subQ2=makeQuery(id+"F0.imprint","INTERSECT",VERTEX,{"derivedFrom":[subQ1,subQ0]});Q69=makeQuery(id+"F0.imprint","IMPRINT",FACE,{"disambiguationData":[TD([[makeQuery(id+"F0.imprint","IMPRINT",EDGE,{"disambiguationData":[TD([[subQ2,-1.0]])],"derivedFrom":subQ1}),-1.0]])]});}
            var Q70;
            {var subQ0=sQuery(id+"F0.wireOp",EDGE,"E8");var subQ1=sQuery(id+"F0.wireOp",EDGE,"E0");var subQ2=makeQuery(id+"F0.imprint","INTERSECT",VERTEX,{"derivedFrom":[subQ1,subQ0]});Q70=makeQuery(id+"F0.imprint","IMPRINT",FACE,{"disambiguationData":[TD([[makeQuery(id+"F0.imprint","IMPRINT",EDGE,{"disambiguationData":[TD([[subQ2,-1.0]])],"derivedFrom":subQ1}),-1.0]])]});}
            var Q71;
            {var subQ0=sQuery(id+"F0.wireOp",EDGE,"E17");var subQ1=sQuery(id+"F0.wireOp",EDGE,"E10");var subQ2=makeQuery(id+"F0.imprint","INTERSECT",VERTEX,{"derivedFrom":[subQ1,subQ0]});Q71=makeQuery(id+"F0.imprint","IMPRINT",FACE,{"disambiguationData":[TD([[makeQuery(id+"F0.imprint","IMPRINT",EDGE,{"disambiguationData":[TD([[subQ2,-1.0]])],"derivedFrom":subQ1}),-1.0]])]});}
            var Q72;
            {var subQ0=sQuery(id+"F0.wireOp",EDGE,"E19");var subQ1=sQuery(id+"F0.wireOp",EDGE,"E1");var subQ2=makeQuery(id+"F0.imprint","INTERSECT",VERTEX,{"derivedFrom":[subQ1,subQ0]});Q72=makeQuery(id+"F0.imprint","IMPRINT",FACE,{"disambiguationData":[TD([[makeQuery(id+"F0.imprint","IMPRINT",EDGE,{"disambiguationData":[TD([[subQ2,-1.0]])],"derivedFrom":subQ1}),1.0]])]});}
            var Q73;
            {var subQ0=sQuery(id+"F0.wireOp",EDGE,"E11");var subQ1=sQuery(id+"F0.wireOp",EDGE,"E8");var subQ2=makeQuery(id+"F0.imprint","INTERSECT",VERTEX,{"derivedFrom":[subQ1,subQ0]});Q73=makeQuery(id+"F0.imprint","IMPRINT",FACE,{"disambiguationData":[TD([[makeQuery(id+"F0.imprint","IMPRINT",EDGE,{"disambiguationData":[TD([[subQ2,-1.0]])],"derivedFrom":subQ1}),-1.0]])]});}
            var Q74;
            {var subQ0=sQuery(id+"F0.wireOp",EDGE,"E17");var subQ1=sQuery(id+"F0.wireOp",EDGE,"E4");var subQ2=makeQuery(id+"F0.imprint","INTERSECT",VERTEX,{"derivedFrom":[subQ1,subQ0]});Q74=makeQuery(id+"F0.imprint","IMPRINT",FACE,{"disambiguationData":[TD([[makeQuery(id+"F0.imprint","IMPRINT",EDGE,{"disambiguationData":[TD([[subQ2,-1.0]])],"derivedFrom":subQ1}),-1.0]])]});}
            var Q75;
            {var subQ0=sQuery(id+"F0.wireOp",EDGE,"E9");var subQ1=sQuery(id+"F0.wireOp",EDGE,"E1");var subQ2=makeQuery(id+"F0.imprint","INTERSECT",VERTEX,{"derivedFrom":[subQ1,subQ0]});Q75=makeQuery(id+"F0.imprint","IMPRINT",FACE,{"disambiguationData":[TD([[makeQuery(id+"F0.imprint","IMPRINT",EDGE,{"disambiguationData":[TD([[subQ2,-1.0]])],"derivedFrom":subQ1}),-1.0]])]});}
            var Q76;
            {var subQ0=sQuery(id+"F0.wireOp",EDGE,"E18");var subQ1=sQuery(id+"F0.wireOp",EDGE,"E11");var subQ2=makeQuery(id+"F0.imprint","INTERSECT",VERTEX,{"derivedFrom":[subQ1,subQ0]});Q76=makeQuery(id+"F0.imprint","IMPRINT",FACE,{"disambiguationData":[TD([[makeQuery(id+"F0.imprint","IMPRINT",EDGE,{"disambiguationData":[TD([[subQ2,-1.0]])],"derivedFrom":subQ1}),-1.0]])]});}
            var Q77;
            {var subQ0=sQuery(id+"F0.wireOp",EDGE,"E20");var subQ1=sQuery(id+"F0.wireOp",EDGE,"E2");var subQ2=makeQuery(id+"F0.imprint","INTERSECT",VERTEX,{"derivedFrom":[subQ1,subQ0]});Q77=makeQuery(id+"F0.imprint","IMPRINT",FACE,{"disambiguationData":[TD([[makeQuery(id+"F0.imprint","IMPRINT",EDGE,{"disambiguationData":[TD([[subQ2,-1.0]])],"derivedFrom":subQ1}),1.0]])]});}
            var Q78;
            {var subQ0=sQuery(id+"F0.wireOp",EDGE,"E12");var subQ1=sQuery(id+"F0.wireOp",EDGE,"E9");var subQ2=makeQuery(id+"F0.imprint","INTERSECT",VERTEX,{"derivedFrom":[subQ1,subQ0]});Q78=makeQuery(id+"F0.imprint","IMPRINT",FACE,{"disambiguationData":[TD([[makeQuery(id+"F0.imprint","IMPRINT",EDGE,{"disambiguationData":[TD([[subQ2,-1.0]])],"derivedFrom":subQ1}),-1.0]])]});}
            var Q79;
            {var subQ0=sQuery(id+"F0.wireOp",EDGE,"E7");var subQ1=sQuery(id+"F0.wireOp",EDGE,"E4");var subQ2=makeQuery(id+"F0.imprint","INTERSECT",VERTEX,{"derivedFrom":[subQ1,subQ0]});Q79=makeQuery(id+"F0.imprint","IMPRINT",FACE,{"disambiguationData":[TD([[makeQuery(id+"F0.imprint","IMPRINT",EDGE,{"disambiguationData":[TD([[subQ2,-1.0]])],"derivedFrom":subQ1}),-1.0]])]});}
            var Q80;
            {var subQ0=sQuery(id+"F0.wireOp",EDGE,"E23");var subQ1=sQuery(id+"F0.wireOp",EDGE,"E2");var subQ2=makeQuery(id+"F0.imprint","INTERSECT",VERTEX,{"derivedFrom":[subQ1,subQ0]});Q80=makeQuery(id+"F0.imprint","IMPRINT",FACE,{"disambiguationData":[TD([[makeQuery(id+"F0.imprint","IMPRINT",EDGE,{"disambiguationData":[TD([[subQ2,-1.0]])],"derivedFrom":subQ1}),-1.0]])]});}
            var Q81;
            {var subQ0=sQuery(id+"F0.wireOp",EDGE,"E14");var subQ1=sQuery(id+"F0.wireOp",EDGE,"E6");var subQ2=makeQuery(id+"F0.imprint","INTERSECT",VERTEX,{"derivedFrom":[subQ1,subQ0]});Q81=makeQuery(id+"F0.imprint","IMPRINT",FACE,{"disambiguationData":[TD([[makeQuery(id+"F0.imprint","IMPRINT",EDGE,{"disambiguationData":[TD([[subQ2,-1.0]])],"derivedFrom":subQ1}),-1.0]])]});}
            var Q82;
            {var subQ0=sQuery(id+"F0.wireOp",EDGE,"E4");var subQ1=sQuery(id+"F0.wireOp",EDGE,"E1");var subQ2=makeQuery(id+"F0.imprint","INTERSECT",VERTEX,{"derivedFrom":[subQ1,subQ0]});Q82=makeQuery(id+"F0.imprint","IMPRINT",FACE,{"disambiguationData":[TD([[makeQuery(id+"F0.imprint","IMPRINT",EDGE,{"disambiguationData":[TD([[subQ2,-1.0]])],"derivedFrom":subQ1}),1.0]])]});}
            var Q83;
            {var subQ0=sQuery(id+"F0.wireOp",EDGE,"E15");var subQ1=sQuery(id+"F0.wireOp",EDGE,"E1");var subQ2=makeQuery(id+"F0.imprint","INTERSECT",VERTEX,{"derivedFrom":[subQ1,subQ0]});Q83=makeQuery(id+"F0.imprint","IMPRINT",FACE,{"disambiguationData":[TD([[makeQuery(id+"F0.imprint","IMPRINT",EDGE,{"disambiguationData":[TD([[subQ2,-1.0]])],"derivedFrom":subQ1}),-1.0]])]});}
            var Q84;
            {var subQ0=sQuery(id+"F0.wireOp",EDGE,"E13");var subQ1=sQuery(id+"F0.wireOp",EDGE,"E5");var subQ2=makeQuery(id+"F0.imprint","INTERSECT",VERTEX,{"derivedFrom":[subQ1,subQ0]});Q84=makeQuery(id+"F0.imprint","IMPRINT",FACE,{"disambiguationData":[TD([[makeQuery(id+"F0.imprint","IMPRINT",EDGE,{"disambiguationData":[TD([[subQ2,-1.0]])],"derivedFrom":subQ1}),-1.0]])]});}
            var Q85;
            {var subQ0=sQuery(id+"F0.wireOp",EDGE,"E3");var subQ1=sQuery(id+"F0.wireOp",EDGE,"E0");var subQ2=makeQuery(id+"F0.imprint","INTERSECT",VERTEX,{"derivedFrom":[subQ1,subQ0]});Q85=makeQuery(id+"F0.imprint","IMPRINT",FACE,{"disambiguationData":[TD([[makeQuery(id+"F0.imprint","IMPRINT",EDGE,{"disambiguationData":[TD([[subQ2,-1.0]])],"derivedFrom":subQ1}),1.0]])]});}
            var Q86;
            {var subQ0=sQuery(id+"F0.wireOp",EDGE,"E15");var subQ1=sQuery(id+"F0.wireOp",EDGE,"E12");var subQ2=makeQuery(id+"F0.imprint","INTERSECT",VERTEX,{"derivedFrom":[subQ1,subQ0]});Q86=makeQuery(id+"F0.imprint","IMPRINT",FACE,{"disambiguationData":[TD([[makeQuery(id+"F0.imprint","IMPRINT",EDGE,{"disambiguationData":[TD([[subQ2,-1.0]])],"derivedFrom":subQ1}),-1.0]])]});}
            var Q87;
            {var subQ0=sQuery(id+"F0.wireOp",EDGE,"E5");var subQ1=sQuery(id+"F0.wireOp",EDGE,"E2");var subQ2=makeQuery(id+"F0.imprint","INTERSECT",VERTEX,{"derivedFrom":[subQ1,subQ0]});Q87=makeQuery(id+"F0.imprint","IMPRINT",FACE,{"disambiguationData":[TD([[makeQuery(id+"F0.imprint","IMPRINT",EDGE,{"disambiguationData":[TD([[subQ2,-1.0]])],"derivedFrom":subQ1}),-1.0]])]});}
            var Q88;
            {var subQ0=sQuery(id+"F0.wireOp",EDGE,"E18");var subQ1=sQuery(id+"F0.wireOp",EDGE,"E0");var subQ2=makeQuery(id+"F0.imprint","INTERSECT",VERTEX,{"derivedFrom":[subQ1,subQ0]});Q88=makeQuery(id+"F0.imprint","IMPRINT",FACE,{"disambiguationData":[TD([[makeQuery(id+"F0.imprint","IMPRINT",EDGE,{"disambiguationData":[TD([[subQ2,-1.0]])],"derivedFrom":subQ1}),-1.0]])]});}
            var Q89;
            {var subQ0=sQuery(id+"F0.wireOp",EDGE,"E9");var subQ1=sQuery(id+"F0.wireOp",EDGE,"E0");var subQ2=makeQuery(id+"F0.imprint","INTERSECT",VERTEX,{"derivedFrom":[subQ1,subQ0]});Q89=makeQuery(id+"F0.imprint","IMPRINT",FACE,{"disambiguationData":[TD([[makeQuery(id+"F0.imprint","IMPRINT",EDGE,{"disambiguationData":[TD([[subQ2,-1.0]])],"derivedFrom":subQ1}),-1.0]])]});}
            var Q90;
            {var subQ0=sQuery(id+"F0.wireOp",EDGE,"E23");var subQ1=sQuery(id+"F0.wireOp",EDGE,"E7");var subQ2=makeQuery(id+"F0.imprint","INTERSECT",VERTEX,{"derivedFrom":[subQ1,subQ0]});Q90=makeQuery(id+"F0.imprint","IMPRINT",FACE,{"disambiguationData":[TD([[makeQuery(id+"F0.imprint","IMPRINT",EDGE,{"disambiguationData":[TD([[subQ2,-1.0]])],"derivedFrom":subQ1}),1.0]])]});}
            var Q91;
            {var subQ0=sQuery(id+"F0.wireOp",EDGE,"E22");var subQ1=sQuery(id+"F0.wireOp",EDGE,"E1");var subQ2=makeQuery(id+"F0.imprint","INTERSECT",VERTEX,{"derivedFrom":[subQ1,subQ0]});Q91=makeQuery(id+"F0.imprint","IMPRINT",FACE,{"disambiguationData":[TD([[makeQuery(id+"F0.imprint","IMPRINT",EDGE,{"disambiguationData":[TD([[subQ2,1.0]])],"derivedFrom":subQ1}),-1.0]])]});}
            var Q92;
            {var subQ0=sQuery(id+"F0.wireOp",EDGE,"E13");var subQ1=sQuery(id+"F0.wireOp",EDGE,"E4");var subQ2=makeQuery(id+"F0.imprint","INTERSECT",VERTEX,{"derivedFrom":[subQ1,subQ0]});Q92=makeQuery(id+"F0.imprint","IMPRINT",FACE,{"disambiguationData":[TD([[makeQuery(id+"F0.imprint","IMPRINT",EDGE,{"disambiguationData":[TD([[subQ2,-1.0]])],"derivedFrom":subQ1}),1.0]])]});}
            var Q93;
            {var subQ0=sQuery(id+"F0.wireOp",EDGE,"E11");var subQ1=sQuery(id+"F0.wireOp",EDGE,"E3");var subQ2=makeQuery(id+"F0.imprint","INTERSECT",VERTEX,{"derivedFrom":[subQ1,subQ0]});Q93=makeQuery(id+"F0.imprint","IMPRINT",FACE,{"disambiguationData":[TD([[makeQuery(id+"F0.imprint","IMPRINT",EDGE,{"disambiguationData":[TD([[subQ2,-1.0]])],"derivedFrom":subQ1}),1.0]])]});}
            var Q94;
            {var subQ0=sQuery(id+"F0.wireOp",EDGE,"E5");var subQ1=sQuery(id+"F0.wireOp",EDGE,"E1");var subQ2=makeQuery(id+"F0.imprint","INTERSECT",VERTEX,{"derivedFrom":[subQ1,subQ0]});Q94=makeQuery(id+"F0.imprint","IMPRINT",FACE,{"disambiguationData":[TD([[makeQuery(id+"F0.imprint","IMPRINT",EDGE,{"disambiguationData":[TD([[subQ2,-1.0]])],"derivedFrom":subQ1}),-1.0]])]});}
            var Q95;
            {var subQ0=sQuery(id+"F0.wireOp",EDGE,"E16");var subQ1=sQuery(id+"F0.wireOp",EDGE,"E8");var subQ2=makeQuery(id+"F0.imprint","INTERSECT",VERTEX,{"derivedFrom":[subQ1,subQ0]});Q95=makeQuery(id+"F0.imprint","IMPRINT",FACE,{"disambiguationData":[TD([[makeQuery(id+"F0.imprint","IMPRINT",EDGE,{"disambiguationData":[TD([[subQ2,-1.0]])],"derivedFrom":subQ1}),1.0]])]});}
            var Q96;
            {var subQ0=sQuery(id+"F0.wireOp",EDGE,"E19");var subQ1=sQuery(id+"F0.wireOp",EDGE,"E2");var subQ2=makeQuery(id+"F0.imprint","INTERSECT",VERTEX,{"derivedFrom":[subQ1,subQ0]});Q96=makeQuery(id+"F0.imprint","IMPRINT",FACE,{"disambiguationData":[TD([[makeQuery(id+"F0.imprint","IMPRINT",EDGE,{"disambiguationData":[TD([[subQ2,1.0]])],"derivedFrom":subQ1}),-1.0]])]});}
            var Q97;
            {var subQ0=sQuery(id+"F0.wireOp",EDGE,"E13");var subQ1=sQuery(id+"F0.wireOp",EDGE,"E0");var subQ2=makeQuery(id+"F0.imprint","INTERSECT",VERTEX,{"derivedFrom":[subQ1,subQ0]});Q97=makeQuery(id+"F0.imprint","IMPRINT",FACE,{"disambiguationData":[TD([[makeQuery(id+"F0.imprint","IMPRINT",EDGE,{"disambiguationData":[TD([[subQ2,-1.0]])],"derivedFrom":subQ1}),1.0]])]});}
            var Q98;
            {var subQ0=sQuery(id+"F0.wireOp",EDGE,"E18");var subQ1=sQuery(id+"F0.wireOp",EDGE,"E16");var subQ2=makeQuery(id+"F0.imprint","INTERSECT",VERTEX,{"derivedFrom":[subQ1,subQ0]});Q98=makeQuery(id+"F0.imprint","IMPRINT",FACE,{"disambiguationData":[TD([[makeQuery(id+"F0.imprint","IMPRINT",EDGE,{"disambiguationData":[TD([[subQ2,-1.0]])],"derivedFrom":subQ1}),1.0]])]});}
            var Q99;
            {var subQ0=sQuery(id+"F0.wireOp",EDGE,"E12");var subQ1=sQuery(id+"F0.wireOp",EDGE,"E2");var subQ2=makeQuery(id+"F0.imprint","INTERSECT",VERTEX,{"derivedFrom":[subQ1,subQ0]});Q99=makeQuery(id+"F0.imprint","IMPRINT",FACE,{"disambiguationData":[TD([[makeQuery(id+"F0.imprint","IMPRINT",EDGE,{"disambiguationData":[TD([[subQ2,-1.0]])],"derivedFrom":subQ1}),1.0]])]});}
            var Q100;
            {var subQ0=sQuery(id+"F0.wireOp",EDGE,"E16");var subQ1=sQuery(id+"F0.wireOp",EDGE,"E2");var subQ2=makeQuery(id+"F0.imprint","INTERSECT",VERTEX,{"derivedFrom":[subQ1,subQ0]});Q100=makeQuery(id+"F0.imprint","IMPRINT",FACE,{"disambiguationData":[TD([[makeQuery(id+"F0.imprint","IMPRINT",EDGE,{"disambiguationData":[TD([[subQ2,-1.0]])],"derivedFrom":subQ1}),1.0]])]});}
            var Q101;
            {var subQ0=sQuery(id+"F0.wireOp",EDGE,"E12");var subQ1=sQuery(id+"F0.wireOp",EDGE,"E2");var subQ2=makeQuery(id+"F0.imprint","INTERSECT",VERTEX,{"derivedFrom":[subQ1,subQ0]});Q101=makeQuery(id+"F0.imprint","IMPRINT",FACE,{"disambiguationData":[TD([[makeQuery(id+"F0.imprint","IMPRINT",EDGE,{"disambiguationData":[TD([[subQ2,-1.0]])],"derivedFrom":subQ1}),-1.0]])]});}
            var Q102;
            {var subQ0=sQuery(id+"F0.wireOp",EDGE,"E22");var subQ1=sQuery(id+"F0.wireOp",EDGE,"E0");var subQ2=makeQuery(id+"F0.imprint","INTERSECT",VERTEX,{"derivedFrom":[subQ1,subQ0]});Q102=makeQuery(id+"F0.imprint","IMPRINT",FACE,{"disambiguationData":[TD([[makeQuery(id+"F0.imprint","IMPRINT",EDGE,{"disambiguationData":[TD([[subQ2,-1.0]])],"derivedFrom":subQ1}),-1.0]])]});}
            var Q103;
            {var subQ0=sQuery(id+"F0.wireOp",EDGE,"E16");var subQ1=sQuery(id+"F0.wireOp",EDGE,"E2");var subQ2=makeQuery(id+"F0.imprint","INTERSECT",VERTEX,{"derivedFrom":[subQ1,subQ0]});Q103=makeQuery(id+"F0.imprint","IMPRINT",FACE,{"disambiguationData":[TD([[makeQuery(id+"F0.imprint","IMPRINT",EDGE,{"disambiguationData":[TD([[subQ2,-1.0]])],"derivedFrom":subQ1}),-1.0]])]});}
            var Q104;
            {var subQ0=sQuery(id+"F0.wireOp",EDGE,"E14");var subQ1=sQuery(id+"F0.wireOp",EDGE,"E12");var subQ2=makeQuery(id+"F0.imprint","INTERSECT",VERTEX,{"derivedFrom":[subQ1,subQ0]});Q104=makeQuery(id+"F0.imprint","IMPRINT",FACE,{"disambiguationData":[TD([[makeQuery(id+"F0.imprint","IMPRINT",EDGE,{"disambiguationData":[TD([[subQ2,-1.0]])],"derivedFrom":subQ1}),1.0]])]});}
            var Q105;
            {var subQ0=sQuery(id+"F0.wireOp",EDGE,"E9");var subQ1=sQuery(id+"F0.wireOp",EDGE,"E7");var subQ2=makeQuery(id+"F0.imprint","INTERSECT",VERTEX,{"derivedFrom":[subQ1,subQ0]});Q105=makeQuery(id+"F0.imprint","IMPRINT",FACE,{"disambiguationData":[TD([[makeQuery(id+"F0.imprint","IMPRINT",EDGE,{"disambiguationData":[TD([[subQ2,-1.0]])],"derivedFrom":subQ1}),1.0]])]});}
            var Q106;
            {var subQ0=sQuery(id+"F0.wireOp",EDGE,"E4");var subQ1=sQuery(id+"F0.wireOp",EDGE,"E2");var subQ2=makeQuery(id+"F0.imprint","INTERSECT",VERTEX,{"derivedFrom":[subQ1,subQ0]});Q106=makeQuery(id+"F0.imprint","IMPRINT",FACE,{"disambiguationData":[TD([[makeQuery(id+"F0.imprint","IMPRINT",EDGE,{"disambiguationData":[TD([[subQ2,-1.0]])],"derivedFrom":subQ1}),1.0]])]});}
            var Q107;
            {var subQ0=sQuery(id+"F0.wireOp",EDGE,"E20");var subQ1=sQuery(id+"F0.wireOp",EDGE,"E2");var subQ2=makeQuery(id+"F0.imprint","INTERSECT",VERTEX,{"derivedFrom":[subQ1,subQ0]});Q107=makeQuery(id+"F0.imprint","IMPRINT",FACE,{"disambiguationData":[TD([[makeQuery(id+"F0.imprint","IMPRINT",EDGE,{"disambiguationData":[TD([[subQ2,-1.0]])],"derivedFrom":subQ1}),-1.0]])]});}
            var Q108;
            {var subQ0=sQuery(id+"F0.wireOp",EDGE,"E14");var subQ1=sQuery(id+"F0.wireOp",EDGE,"E11");var subQ2=makeQuery(id+"F0.imprint","INTERSECT",VERTEX,{"derivedFrom":[subQ1,subQ0]});Q108=makeQuery(id+"F0.imprint","IMPRINT",FACE,{"disambiguationData":[TD([[makeQuery(id+"F0.imprint","IMPRINT",EDGE,{"disambiguationData":[TD([[subQ2,-1.0]])],"derivedFrom":subQ1}),-1.0]])]});}
            var Q109;
            {var subQ0=sQuery(id+"F0.wireOp",EDGE,"E9");var subQ1=sQuery(id+"F0.wireOp",EDGE,"E6");var subQ2=makeQuery(id+"F0.imprint","INTERSECT",VERTEX,{"derivedFrom":[subQ1,subQ0]});Q109=makeQuery(id+"F0.imprint","IMPRINT",FACE,{"disambiguationData":[TD([[makeQuery(id+"F0.imprint","IMPRINT",EDGE,{"disambiguationData":[TD([[subQ2,-1.0]])],"derivedFrom":subQ1}),-1.0]])]});}
            var Q110;
            {var subQ0=sQuery(id+"F0.wireOp",EDGE,"E20");var subQ1=sQuery(id+"F0.wireOp",EDGE,"E1");var subQ2=makeQuery(id+"F0.imprint","INTERSECT",VERTEX,{"derivedFrom":[subQ1,subQ0]});Q110=makeQuery(id+"F0.imprint","IMPRINT",FACE,{"disambiguationData":[TD([[makeQuery(id+"F0.imprint","IMPRINT",EDGE,{"disambiguationData":[TD([[subQ2,-1.0]])],"derivedFrom":subQ1}),1.0]])]});}
            var Q111;
            {var subQ0=sQuery(id+"F0.wireOp",EDGE,"E23");var subQ1=sQuery(id+"F0.wireOp",EDGE,"E13");var subQ2=makeQuery(id+"F0.imprint","INTERSECT",VERTEX,{"derivedFrom":[subQ1,subQ0]});Q111=makeQuery(id+"F0.imprint","IMPRINT",FACE,{"disambiguationData":[TD([[makeQuery(id+"F0.imprint","IMPRINT",EDGE,{"disambiguationData":[TD([[subQ2,-1.0]])],"derivedFrom":subQ1}),-1.0]])]});}
            var Q112;
            {var subQ0=sQuery(id+"F0.wireOp",EDGE,"E19");var subQ1=sQuery(id+"F0.wireOp",EDGE,"E1");var subQ2=makeQuery(id+"F0.imprint","INTERSECT",VERTEX,{"derivedFrom":[subQ1,subQ0]});Q112=makeQuery(id+"F0.imprint","IMPRINT",FACE,{"disambiguationData":[TD([[makeQuery(id+"F0.imprint","IMPRINT",EDGE,{"disambiguationData":[TD([[subQ2,-1.0]])],"derivedFrom":subQ1}),-1.0]])]});}
            var Q113;
            {var subQ0=sQuery(id+"F0.wireOp",EDGE,"E17");var subQ1=sQuery(id+"F0.wireOp",EDGE,"E15");var subQ2=makeQuery(id+"F0.imprint","INTERSECT",VERTEX,{"derivedFrom":[subQ1,subQ0]});Q113=makeQuery(id+"F0.imprint","IMPRINT",FACE,{"disambiguationData":[TD([[makeQuery(id+"F0.imprint","IMPRINT",EDGE,{"disambiguationData":[TD([[subQ2,-1.0]])],"derivedFrom":subQ1}),-1.0]])]});}
            var Q114;
            {var subQ0=sQuery(id+"F0.wireOp",EDGE,"E15");var subQ1=sQuery(id+"F0.wireOp",EDGE,"E13");var subQ2=makeQuery(id+"F0.imprint","INTERSECT",VERTEX,{"derivedFrom":[subQ1,subQ0]});Q114=makeQuery(id+"F0.imprint","IMPRINT",FACE,{"disambiguationData":[TD([[makeQuery(id+"F0.imprint","IMPRINT",EDGE,{"disambiguationData":[TD([[subQ2,-1.0]])],"derivedFrom":subQ1}),1.0]])]});}
            var Q115;
            {var subQ0=sQuery(id+"F0.wireOp",EDGE,"E10");var subQ1=sQuery(id+"F0.wireOp",EDGE,"E3");var subQ2=makeQuery(id+"F0.imprint","INTERSECT",VERTEX,{"derivedFrom":[subQ1,subQ0]});Q115=makeQuery(id+"F0.imprint","IMPRINT",FACE,{"disambiguationData":[TD([[makeQuery(id+"F0.imprint","IMPRINT",EDGE,{"disambiguationData":[TD([[subQ2,-1.0]])],"derivedFrom":subQ1}),1.0]])]});}
            var Q116;
            {var subQ0=sQuery(id+"F0.wireOp",EDGE,"E14");var subQ1=sQuery(id+"F0.wireOp",EDGE,"E7");var subQ2=makeQuery(id+"F0.imprint","INTERSECT",VERTEX,{"derivedFrom":[subQ1,subQ0]});Q116=makeQuery(id+"F0.imprint","IMPRINT",FACE,{"disambiguationData":[TD([[makeQuery(id+"F0.imprint","IMPRINT",EDGE,{"disambiguationData":[TD([[subQ2,-1.0]])],"derivedFrom":subQ1}),1.0]])]});}
            var Q117;
            {var subQ0=sQuery(id+"F0.wireOp",EDGE,"E9");var subQ1=sQuery(id+"F0.wireOp",EDGE,"E2");var subQ2=makeQuery(id+"F0.imprint","INTERSECT",VERTEX,{"derivedFrom":[subQ1,subQ0]});Q117=makeQuery(id+"F0.imprint","IMPRINT",FACE,{"disambiguationData":[TD([[makeQuery(id+"F0.imprint","IMPRINT",EDGE,{"disambiguationData":[TD([[subQ2,-1.0]])],"derivedFrom":subQ1}),1.0]])]});}
            var Q118;
            {var subQ0=sQuery(id+"F0.wireOp",EDGE,"E4");var subQ1=sQuery(id+"F0.wireOp",EDGE,"E2");var subQ2=makeQuery(id+"F0.imprint","INTERSECT",VERTEX,{"derivedFrom":[subQ1,subQ0]});Q118=makeQuery(id+"F0.imprint","IMPRINT",FACE,{"disambiguationData":[TD([[makeQuery(id+"F0.imprint","IMPRINT",EDGE,{"disambiguationData":[TD([[subQ2,-1.0]])],"derivedFrom":subQ1}),-1.0]])]});}
            var Q119;
            {var subQ0=sQuery(id+"F0.wireOp",EDGE,"E23");var subQ1=sQuery(id+"F0.wireOp",EDGE,"E18");var subQ2=makeQuery(id+"F0.imprint","INTERSECT",VERTEX,{"derivedFrom":[subQ1,subQ0]});Q119=makeQuery(id+"F0.imprint","IMPRINT",FACE,{"disambiguationData":[TD([[makeQuery(id+"F0.imprint","IMPRINT",EDGE,{"disambiguationData":[TD([[subQ2,-1.0]])],"derivedFrom":subQ1}),1.0]])]});}
            var Q120;
            {var subQ0=sQuery(id+"F0.wireOp",EDGE,"E23");var subQ1=sQuery(id+"F0.wireOp",EDGE,"E14");var subQ2=makeQuery(id+"F0.imprint","INTERSECT",VERTEX,{"derivedFrom":[subQ1,subQ0]});Q120=makeQuery(id+"F0.imprint","IMPRINT",FACE,{"disambiguationData":[TD([[makeQuery(id+"F0.imprint","IMPRINT",EDGE,{"disambiguationData":[TD([[subQ2,-1.0]])],"derivedFrom":subQ1}),1.0]])]});}
            var Q121;
            {var subQ0=sQuery(id+"F0.wireOp",EDGE,"E11");var subQ1=sQuery(id+"F0.wireOp",EDGE,"E9");var subQ2=makeQuery(id+"F0.imprint","INTERSECT",VERTEX,{"derivedFrom":[subQ1,subQ0]});Q121=makeQuery(id+"F0.imprint","IMPRINT",FACE,{"disambiguationData":[TD([[makeQuery(id+"F0.imprint","IMPRINT",EDGE,{"disambiguationData":[TD([[subQ2,-1.0]])],"derivedFrom":subQ1}),1.0]])]});}
            var Q122;
            {var subQ0=sQuery(id+"F0.wireOp",EDGE,"E4");var subQ1=sQuery(id+"F0.wireOp",EDGE,"E1");var subQ2=makeQuery(id+"F0.imprint","INTERSECT",VERTEX,{"derivedFrom":[subQ1,subQ0]});Q122=makeQuery(id+"F0.imprint","IMPRINT",FACE,{"disambiguationData":[TD([[makeQuery(id+"F0.imprint","IMPRINT",EDGE,{"disambiguationData":[TD([[subQ2,-1.0]])],"derivedFrom":subQ1}),-1.0]])]});}
            var Q123;
            {var subQ0=sQuery(id+"F0.wireOp",EDGE,"E6");var subQ1=sQuery(id+"F0.wireOp",EDGE,"E4");var subQ2=makeQuery(id+"F0.imprint","INTERSECT",VERTEX,{"derivedFrom":[subQ1,subQ0]});Q123=makeQuery(id+"F0.imprint","IMPRINT",FACE,{"disambiguationData":[TD([[makeQuery(id+"F0.imprint","IMPRINT",EDGE,{"disambiguationData":[TD([[subQ2,-1.0]])],"derivedFrom":subQ1}),1.0]])]});}
            var Q124;
            {var subQ0=sQuery(id+"F0.wireOp",EDGE,"E20");var subQ1=sQuery(id+"F0.wireOp",EDGE,"E1");var subQ2=makeQuery(id+"F0.imprint","INTERSECT",VERTEX,{"derivedFrom":[subQ1,subQ0]});Q124=makeQuery(id+"F0.imprint","IMPRINT",FACE,{"disambiguationData":[TD([[makeQuery(id+"F0.imprint","IMPRINT",EDGE,{"disambiguationData":[TD([[subQ2,-1.0]])],"derivedFrom":subQ1}),-1.0]])]});}
            var Q125;
            {var subQ0=sQuery(id+"F0.wireOp",EDGE,"E23");var subQ1=sQuery(id+"F0.wireOp",EDGE,"E1");var subQ2=makeQuery(id+"F0.imprint","INTERSECT",VERTEX,{"derivedFrom":[subQ1,subQ0]});Q125=makeQuery(id+"F0.imprint","IMPRINT",FACE,{"disambiguationData":[TD([[makeQuery(id+"F0.imprint","IMPRINT",EDGE,{"disambiguationData":[TD([[subQ2,-1.0]])],"derivedFrom":subQ1}),1.0]])]});}
            var Q126;
            {var subQ0=sQuery(id+"F0.wireOp",EDGE,"E23");var subQ1=sQuery(id+"F0.wireOp",EDGE,"E17");var subQ2=makeQuery(id+"F0.imprint","INTERSECT",VERTEX,{"derivedFrom":[subQ1,subQ0]});Q126=makeQuery(id+"F0.imprint","IMPRINT",FACE,{"disambiguationData":[TD([[makeQuery(id+"F0.imprint","IMPRINT",EDGE,{"disambiguationData":[TD([[subQ2,-1.0]])],"derivedFrom":subQ1}),-1.0]])]});}
            var Q127;
            {var subQ0=sQuery(id+"F0.wireOp",EDGE,"E17");var subQ1=sQuery(id+"F0.wireOp",EDGE,"E11");var subQ2=makeQuery(id+"F0.imprint","INTERSECT",VERTEX,{"derivedFrom":[subQ1,subQ0]});Q127=makeQuery(id+"F0.imprint","IMPRINT",FACE,{"disambiguationData":[TD([[makeQuery(id+"F0.imprint","IMPRINT",EDGE,{"disambiguationData":[TD([[subQ2,-1.0]])],"derivedFrom":subQ1}),1.0]])]});}
            var Q128;
            {var subQ0=sQuery(id+"F0.wireOp",EDGE,"E13");var subQ1=sQuery(id+"F0.wireOp",EDGE,"E11");var subQ2=makeQuery(id+"F0.imprint","INTERSECT",VERTEX,{"derivedFrom":[subQ1,subQ0]});Q128=makeQuery(id+"F0.imprint","IMPRINT",FACE,{"disambiguationData":[TD([[makeQuery(id+"F0.imprint","IMPRINT",EDGE,{"disambiguationData":[TD([[subQ2,-1.0]])],"derivedFrom":subQ1}),1.0]])]});}
            var Q129;
            {var subQ0=sQuery(id+"F0.wireOp",EDGE,"E8");var subQ1=sQuery(id+"F0.wireOp",EDGE,"E6");var subQ2=makeQuery(id+"F0.imprint","INTERSECT",VERTEX,{"derivedFrom":[subQ1,subQ0]});Q129=makeQuery(id+"F0.imprint","IMPRINT",FACE,{"disambiguationData":[TD([[makeQuery(id+"F0.imprint","IMPRINT",EDGE,{"disambiguationData":[TD([[subQ2,-1.0]])],"derivedFrom":subQ1}),1.0]])]});}
            var Q130;
            {var subQ0=sQuery(id+"F0.wireOp",EDGE,"E8");var subQ1=sQuery(id+"F0.wireOp",EDGE,"E1");var subQ2=makeQuery(id+"F0.imprint","INTERSECT",VERTEX,{"derivedFrom":[subQ1,subQ0]});Q130=makeQuery(id+"F0.imprint","IMPRINT",FACE,{"disambiguationData":[TD([[makeQuery(id+"F0.imprint","IMPRINT",EDGE,{"disambiguationData":[TD([[subQ2,-1.0]])],"derivedFrom":subQ1}),1.0]])]});}
            var Q131;
            {var subQ0=sQuery(id+"F0.wireOp",EDGE,"E18");var subQ1=sQuery(id+"F0.wireOp",EDGE,"E4");var subQ2=makeQuery(id+"F0.imprint","INTERSECT",VERTEX,{"derivedFrom":[subQ1,subQ0]});Q131=makeQuery(id+"F0.imprint","IMPRINT",FACE,{"disambiguationData":[TD([[makeQuery(id+"F0.imprint","IMPRINT",EDGE,{"disambiguationData":[TD([[subQ2,-1.0]])],"derivedFrom":subQ1}),1.0]])]});}
            var Q132;
            {var subQ0=sQuery(id+"F0.wireOp",EDGE,"E18");var subQ1=sQuery(id+"F0.wireOp",EDGE,"E4");var subQ2=makeQuery(id+"F0.imprint","INTERSECT",VERTEX,{"derivedFrom":[subQ1,subQ0]});Q132=makeQuery(id+"F0.imprint","IMPRINT",FACE,{"disambiguationData":[TD([[makeQuery(id+"F0.imprint","IMPRINT",EDGE,{"disambiguationData":[TD([[subQ2,-1.0]])],"derivedFrom":subQ1}),-1.0]])]});}
            var Q133;
            {var subQ0=sQuery(id+"F0.wireOp",EDGE,"E14");var subQ1=sQuery(id+"F0.wireOp",EDGE,"E4");var subQ2=makeQuery(id+"F0.imprint","INTERSECT",VERTEX,{"derivedFrom":[subQ1,subQ0]});Q133=makeQuery(id+"F0.imprint","IMPRINT",FACE,{"disambiguationData":[TD([[makeQuery(id+"F0.imprint","IMPRINT",EDGE,{"disambiguationData":[TD([[subQ2,-1.0]])],"derivedFrom":subQ1}),1.0]])]});}
            var Q134;
            {var subQ0=sQuery(id+"F0.wireOp",EDGE,"E18");var subQ1=sQuery(id+"F0.wireOp",EDGE,"E12");var subQ2=makeQuery(id+"F0.imprint","INTERSECT",VERTEX,{"derivedFrom":[subQ1,subQ0]});Q134=makeQuery(id+"F0.imprint","IMPRINT",FACE,{"disambiguationData":[TD([[makeQuery(id+"F0.imprint","IMPRINT",EDGE,{"disambiguationData":[TD([[subQ2,-1.0]])],"derivedFrom":subQ1}),1.0]])]});}
            var Q135;
            {var subQ0=sQuery(id+"F0.wireOp",EDGE,"E14");var subQ1=sQuery(id+"F0.wireOp",EDGE,"E2");var subQ2=makeQuery(id+"F0.imprint","INTERSECT",VERTEX,{"derivedFrom":[subQ1,subQ0]});Q135=makeQuery(id+"F0.imprint","IMPRINT",FACE,{"disambiguationData":[TD([[makeQuery(id+"F0.imprint","IMPRINT",EDGE,{"disambiguationData":[TD([[subQ2,-1.0]])],"derivedFrom":subQ1}),1.0]])]});}
            var Q136;
            {var subQ0=sQuery(id+"F0.wireOp",EDGE,"E9");var subQ1=sQuery(id+"F0.wireOp",EDGE,"E2");var subQ2=makeQuery(id+"F0.imprint","INTERSECT",VERTEX,{"derivedFrom":[subQ1,subQ0]});Q136=makeQuery(id+"F0.imprint","IMPRINT",FACE,{"disambiguationData":[TD([[makeQuery(id+"F0.imprint","IMPRINT",EDGE,{"disambiguationData":[TD([[subQ2,-1.0]])],"derivedFrom":subQ1}),-1.0]])]});}
            var Q137;
            {var subQ0=sQuery(id+"F0.wireOp",EDGE,"E14");var subQ1=sQuery(id+"F0.wireOp",EDGE,"E4");var subQ2=makeQuery(id+"F0.imprint","INTERSECT",VERTEX,{"derivedFrom":[subQ1,subQ0]});Q137=makeQuery(id+"F0.imprint","IMPRINT",FACE,{"disambiguationData":[TD([[makeQuery(id+"F0.imprint","IMPRINT",EDGE,{"disambiguationData":[TD([[subQ2,-1.0]])],"derivedFrom":subQ1}),-1.0]])]});}
            var Q138;
            {var subQ0=sQuery(id+"F0.wireOp",EDGE,"E23");var subQ1=sQuery(id+"F0.wireOp",EDGE,"E9");var subQ2=makeQuery(id+"F0.imprint","INTERSECT",VERTEX,{"derivedFrom":[subQ1,subQ0]});Q138=makeQuery(id+"F0.imprint","IMPRINT",FACE,{"disambiguationData":[TD([[makeQuery(id+"F0.imprint","IMPRINT",EDGE,{"disambiguationData":[TD([[subQ2,-1.0]])],"derivedFrom":subQ1}),1.0]])]});}
            var Q139;
            {var subQ0=sQuery(id+"F0.wireOp",EDGE,"E11");var subQ1=sQuery(id+"F0.wireOp",EDGE,"E4");var subQ2=makeQuery(id+"F0.imprint","INTERSECT",VERTEX,{"derivedFrom":[subQ1,subQ0]});Q139=makeQuery(id+"F0.imprint","IMPRINT",FACE,{"disambiguationData":[TD([[makeQuery(id+"F0.imprint","IMPRINT",EDGE,{"disambiguationData":[TD([[subQ2,-1.0]])],"derivedFrom":subQ1}),1.0]])]});}
            var Q140;
            {var subQ0=sQuery(id+"F0.wireOp",EDGE,"E6");var subQ1=sQuery(id+"F0.wireOp",EDGE,"E4");var subQ2=makeQuery(id+"F0.imprint","INTERSECT",VERTEX,{"derivedFrom":[subQ1,subQ0]});Q140=makeQuery(id+"F0.imprint","IMPRINT",FACE,{"disambiguationData":[TD([[makeQuery(id+"F0.imprint","IMPRINT",EDGE,{"disambiguationData":[TD([[subQ2,-1.0]])],"derivedFrom":subQ1}),-1.0]])]});}
            var Q141;
            {var subQ0=sQuery(id+"F0.wireOp",EDGE,"E11");var subQ1=sQuery(id+"F0.wireOp",EDGE,"E1");var subQ2=makeQuery(id+"F0.imprint","INTERSECT",VERTEX,{"derivedFrom":[subQ1,subQ0]});Q141=makeQuery(id+"F0.imprint","IMPRINT",FACE,{"disambiguationData":[TD([[makeQuery(id+"F0.imprint","IMPRINT",EDGE,{"disambiguationData":[TD([[subQ2,-1.0]])],"derivedFrom":subQ1}),1.0]])]});}
            var Q142;
            {var subQ0=sQuery(id+"F0.wireOp",EDGE,"E13");var subQ1=sQuery(id+"F0.wireOp",EDGE,"E6");var subQ2=makeQuery(id+"F0.imprint","INTERSECT",VERTEX,{"derivedFrom":[subQ1,subQ0]});Q142=makeQuery(id+"F0.imprint","IMPRINT",FACE,{"disambiguationData":[TD([[makeQuery(id+"F0.imprint","IMPRINT",EDGE,{"disambiguationData":[TD([[subQ2,-1.0]])],"derivedFrom":subQ1}),1.0]])]});}
            var Q143;
            {var subQ0=sQuery(id+"F0.wireOp",EDGE,"E6");var subQ1=sQuery(id+"F0.wireOp",EDGE,"E3");var subQ2=makeQuery(id+"F0.imprint","INTERSECT",VERTEX,{"derivedFrom":[subQ1,subQ0]});Q143=makeQuery(id+"F0.imprint","IMPRINT",FACE,{"disambiguationData":[TD([[makeQuery(id+"F0.imprint","IMPRINT",EDGE,{"disambiguationData":[TD([[subQ2,-1.0]])],"derivedFrom":subQ1}),-1.0]])]});}
            var Q144;
            {var subQ0=sQuery(id+"F0.wireOp",EDGE,"E3");var subQ1=sQuery(id+"F0.wireOp",EDGE,"E1");var subQ2=makeQuery(id+"F0.imprint","INTERSECT",VERTEX,{"derivedFrom":[subQ1,subQ0]});Q144=makeQuery(id+"F0.imprint","IMPRINT",FACE,{"disambiguationData":[TD([[makeQuery(id+"F0.imprint","IMPRINT",EDGE,{"disambiguationData":[TD([[subQ2,-1.0]])],"derivedFrom":subQ1}),1.0]])]});}
            var Q145;
            {var subQ0=sQuery(id+"F0.wireOp",EDGE,"E13");var subQ1=sQuery(id+"F0.wireOp",EDGE,"E1");var subQ2=makeQuery(id+"F0.imprint","INTERSECT",VERTEX,{"derivedFrom":[subQ1,subQ0]});Q145=makeQuery(id+"F0.imprint","IMPRINT",FACE,{"disambiguationData":[TD([[makeQuery(id+"F0.imprint","IMPRINT",EDGE,{"disambiguationData":[TD([[subQ2,-1.0]])],"derivedFrom":subQ1}),1.0]])]});}
            var Q146;
            {var subQ0=sQuery(id+"F0.wireOp",EDGE,"E13");var subQ1=sQuery(id+"F0.wireOp",EDGE,"E10");var subQ2=makeQuery(id+"F0.imprint","INTERSECT",VERTEX,{"derivedFrom":[subQ1,subQ0]});Q146=makeQuery(id+"F0.imprint","IMPRINT",FACE,{"disambiguationData":[TD([[makeQuery(id+"F0.imprint","IMPRINT",EDGE,{"disambiguationData":[TD([[subQ2,-1.0]])],"derivedFrom":subQ1}),-1.0]])]});}
            var Q147;
            {var subQ0=sQuery(id+"F0.wireOp",EDGE,"E17");var subQ1=sQuery(id+"F0.wireOp",EDGE,"E3");var subQ2=makeQuery(id+"F0.imprint","INTERSECT",VERTEX,{"derivedFrom":[subQ1,subQ0]});Q147=makeQuery(id+"F0.imprint","IMPRINT",FACE,{"disambiguationData":[TD([[makeQuery(id+"F0.imprint","IMPRINT",EDGE,{"disambiguationData":[TD([[subQ2,-1.0]])],"derivedFrom":subQ1}),1.0]])]});}
            var Q148;
            {var subQ0=sQuery(id+"F0.wireOp",EDGE,"E3");var subQ1=sQuery(id+"F0.wireOp",EDGE,"E1");var subQ2=makeQuery(id+"F0.imprint","INTERSECT",VERTEX,{"derivedFrom":[subQ1,subQ0]});Q148=makeQuery(id+"F0.imprint","IMPRINT",FACE,{"disambiguationData":[TD([[makeQuery(id+"F0.imprint","IMPRINT",EDGE,{"disambiguationData":[TD([[subQ2,-1.0]])],"derivedFrom":subQ1}),-1.0]])]});}
            var Q149;
            {var subQ0=sQuery(id+"F0.wireOp",EDGE,"E17");var subQ1=sQuery(id+"F0.wireOp",EDGE,"E3");var subQ2=makeQuery(id+"F0.imprint","INTERSECT",VERTEX,{"derivedFrom":[subQ1,subQ0]});Q149=makeQuery(id+"F0.imprint","IMPRINT",FACE,{"disambiguationData":[TD([[makeQuery(id+"F0.imprint","IMPRINT",EDGE,{"disambiguationData":[TD([[subQ2,-1.0]])],"derivedFrom":subQ1}),-1.0]])]});}
            var Q150;
            {var subQ0=sQuery(id+"F0.wireOp",EDGE,"E8");var subQ1=sQuery(id+"F0.wireOp",EDGE,"E5");var subQ2=makeQuery(id+"F0.imprint","INTERSECT",VERTEX,{"derivedFrom":[subQ1,subQ0]});Q150=makeQuery(id+"F0.imprint","IMPRINT",FACE,{"disambiguationData":[TD([[makeQuery(id+"F0.imprint","IMPRINT",EDGE,{"disambiguationData":[TD([[subQ2,-1.0]])],"derivedFrom":subQ1}),-1.0]])]});}
            var Q151;
            {var subQ0=sQuery(id+"F0.wireOp",EDGE,"E3");var subQ1=sQuery(id+"F0.wireOp",EDGE,"E0");var subQ2=makeQuery(id+"F0.imprint","INTERSECT",VERTEX,{"derivedFrom":[subQ1,subQ0]});Q151=makeQuery(id+"F0.imprint","IMPRINT",FACE,{"disambiguationData":[TD([[makeQuery(id+"F0.imprint","IMPRINT",EDGE,{"disambiguationData":[TD([[subQ2,-1.0]])],"derivedFrom":subQ1}),-1.0]])]});}
            var Q152;
            {var subQ0=sQuery(id+"F0.wireOp",EDGE,"E19");var subQ1=sQuery(id+"F0.wireOp",EDGE,"E0");var subQ2=makeQuery(id+"F0.imprint","INTERSECT",VERTEX,{"derivedFrom":[subQ1,subQ0]});Q152=makeQuery(id+"F0.imprint","IMPRINT",FACE,{"disambiguationData":[TD([[makeQuery(id+"F0.imprint","IMPRINT",EDGE,{"disambiguationData":[TD([[subQ2,-1.0]])],"derivedFrom":subQ1}),1.0]])]});}
            var Q153;
            {var subQ0=sQuery(id+"F0.wireOp",EDGE,"E7");var subQ1=sQuery(id+"F0.wireOp",EDGE,"E5");var subQ2=makeQuery(id+"F0.imprint","INTERSECT",VERTEX,{"derivedFrom":[subQ1,subQ0]});Q153=makeQuery(id+"F0.imprint","IMPRINT",FACE,{"disambiguationData":[TD([[makeQuery(id+"F0.imprint","IMPRINT",EDGE,{"disambiguationData":[TD([[subQ2,-1.0]])],"derivedFrom":subQ1}),1.0]])]});}
            var Q154;
            {var subQ0=sQuery(id+"F0.wireOp",EDGE,"E2");var subQ1=sQuery(id+"F0.wireOp",EDGE,"E0");var subQ2=makeQuery(id+"F0.imprint","INTERSECT",VERTEX,{"derivedFrom":[subQ1,subQ0]});Q154=makeQuery(id+"F0.imprint","IMPRINT",FACE,{"disambiguationData":[TD([[makeQuery(id+"F0.imprint","IMPRINT",EDGE,{"disambiguationData":[TD([[subQ2,-1.0]])],"derivedFrom":subQ1}),1.0]])]});}
            var Q155;
            {var subQ0=sQuery(id+"F0.wireOp",EDGE,"E7");var subQ1=sQuery(id+"F0.wireOp",EDGE,"E0");var subQ2=makeQuery(id+"F0.imprint","INTERSECT",VERTEX,{"derivedFrom":[subQ1,subQ0]});Q155=makeQuery(id+"F0.imprint","IMPRINT",FACE,{"disambiguationData":[TD([[makeQuery(id+"F0.imprint","IMPRINT",EDGE,{"disambiguationData":[TD([[subQ2,-1.0]])],"derivedFrom":subQ1}),1.0]])]});}
            var Q156;
            {var subQ0=sQuery(id+"F0.wireOp",EDGE,"E12");var subQ1=sQuery(id+"F0.wireOp",EDGE,"E5");var subQ2=makeQuery(id+"F0.imprint","INTERSECT",VERTEX,{"derivedFrom":[subQ1,subQ0]});Q156=makeQuery(id+"F0.imprint","IMPRINT",FACE,{"disambiguationData":[TD([[makeQuery(id+"F0.imprint","IMPRINT",EDGE,{"disambiguationData":[TD([[subQ2,-1.0]])],"derivedFrom":subQ1}),1.0]])]});}
            var Q157;
            {var subQ0=sQuery(id+"F0.wireOp",EDGE,"E16");var subQ1=sQuery(id+"F0.wireOp",EDGE,"E10");var subQ2=makeQuery(id+"F0.imprint","INTERSECT",VERTEX,{"derivedFrom":[subQ1,subQ0]});Q157=makeQuery(id+"F0.imprint","IMPRINT",FACE,{"disambiguationData":[TD([[makeQuery(id+"F0.imprint","IMPRINT",EDGE,{"disambiguationData":[TD([[subQ2,-1.0]])],"derivedFrom":subQ1}),1.0]])]});}
            var Q158;
            {var subQ0=sQuery(id+"F0.wireOp",EDGE,"E10");var subQ1=sQuery(id+"F0.wireOp",EDGE,"E8");var subQ2=makeQuery(id+"F0.imprint","INTERSECT",VERTEX,{"derivedFrom":[subQ1,subQ0]});Q158=makeQuery(id+"F0.imprint","IMPRINT",FACE,{"disambiguationData":[TD([[makeQuery(id+"F0.imprint","IMPRINT",EDGE,{"disambiguationData":[TD([[subQ2,-1.0]])],"derivedFrom":subQ1}),1.0]])]});}
            var Q159;
            {var subQ0=sQuery(id+"F0.wireOp",EDGE,"E15");var subQ1=sQuery(id+"F0.wireOp",EDGE,"E8");var subQ2=makeQuery(id+"F0.imprint","INTERSECT",VERTEX,{"derivedFrom":[subQ1,subQ0]});Q159=makeQuery(id+"F0.imprint","IMPRINT",FACE,{"disambiguationData":[TD([[makeQuery(id+"F0.imprint","IMPRINT",EDGE,{"disambiguationData":[TD([[subQ2,-1.0]])],"derivedFrom":subQ1}),1.0]])]});}
            var Q160;
            {var subQ0=sQuery(id+"F0.wireOp",EDGE,"E8");var subQ1=sQuery(id+"F0.wireOp",EDGE,"E3");var subQ2=makeQuery(id+"F0.imprint","INTERSECT",VERTEX,{"derivedFrom":[subQ1,subQ0]});Q160=makeQuery(id+"F0.imprint","IMPRINT",FACE,{"disambiguationData":[TD([[makeQuery(id+"F0.imprint","IMPRINT",EDGE,{"disambiguationData":[TD([[subQ2,-1.0]])],"derivedFrom":subQ1}),1.0]])]});}
            var Q161;
            {var subQ0=sQuery(id+"F0.wireOp",EDGE,"E12");var subQ1=sQuery(id+"F0.wireOp",EDGE,"E10");var subQ2=makeQuery(id+"F0.imprint","INTERSECT",VERTEX,{"derivedFrom":[subQ1,subQ0]});Q161=makeQuery(id+"F0.imprint","IMPRINT",FACE,{"disambiguationData":[TD([[makeQuery(id+"F0.imprint","IMPRINT",EDGE,{"disambiguationData":[TD([[subQ2,-1.0]])],"derivedFrom":subQ1}),1.0]])]});}
            var Q162;
            {var subQ0=sQuery(id+"F0.wireOp",EDGE,"E16");var subQ1=sQuery(id+"F0.wireOp",EDGE,"E15");var subQ2=makeQuery(id+"F0.imprint","INTERSECT",VERTEX,{"derivedFrom":[subQ1,subQ0]});Q162=makeQuery(id+"F0.imprint","IMPRINT",FACE,{"disambiguationData":[TD([[makeQuery(id+"F0.imprint","IMPRINT",EDGE,{"disambiguationData":[TD([[subQ2,-1.0]])],"derivedFrom":subQ1}),1.0]])]});}
            var Q163;
            {var subQ0=sQuery(id+"F0.wireOp",EDGE,"E19");var subQ1=sQuery(id+"F0.wireOp",EDGE,"E0");var subQ2=makeQuery(id+"F0.imprint","INTERSECT",VERTEX,{"derivedFrom":[subQ1,subQ0]});Q163=makeQuery(id+"F0.imprint","IMPRINT",FACE,{"disambiguationData":[TD([[makeQuery(id+"F0.imprint","IMPRINT",EDGE,{"disambiguationData":[TD([[subQ2,-1.0]])],"derivedFrom":subQ1}),-1.0]])]});}
            var Q164;
            {var subQ0=sQuery(id+"F0.wireOp",EDGE,"E5");var subQ1=sQuery(id+"F0.wireOp",EDGE,"E3");var subQ2=makeQuery(id+"F0.imprint","INTERSECT",VERTEX,{"derivedFrom":[subQ1,subQ0]});Q164=makeQuery(id+"F0.imprint","IMPRINT",FACE,{"disambiguationData":[TD([[makeQuery(id+"F0.imprint","IMPRINT",EDGE,{"disambiguationData":[TD([[subQ2,-1.0]])],"derivedFrom":subQ1}),1.0]])]});}
            var Q165;
            {var subQ0=sQuery(id+"F0.wireOp",EDGE,"E13");var subQ1=sQuery(id+"F0.wireOp",EDGE,"E3");var subQ2=makeQuery(id+"F0.imprint","INTERSECT",VERTEX,{"derivedFrom":[subQ1,subQ0]});Q165=makeQuery(id+"F0.imprint","IMPRINT",FACE,{"disambiguationData":[TD([[makeQuery(id+"F0.imprint","IMPRINT",EDGE,{"disambiguationData":[TD([[subQ2,-1.0]])],"derivedFrom":subQ1}),1.0]])]});}
            var Q166;
            {var subQ0=sQuery(id+"F0.wireOp",EDGE,"E8");var subQ1=sQuery(id+"F0.wireOp",EDGE,"E1");var subQ2=makeQuery(id+"F0.imprint","INTERSECT",VERTEX,{"derivedFrom":[subQ1,subQ0]});Q166=makeQuery(id+"F0.imprint","IMPRINT",FACE,{"disambiguationData":[TD([[makeQuery(id+"F0.imprint","IMPRINT",EDGE,{"disambiguationData":[TD([[subQ2,-1.0]])],"derivedFrom":subQ1}),-1.0]])]});}
            var Q167;
            {var subQ0=sQuery(id+"F0.wireOp",EDGE,"E17");var subQ1=sQuery(id+"F0.wireOp",EDGE,"E6");var subQ2=makeQuery(id+"F0.imprint","INTERSECT",VERTEX,{"derivedFrom":[subQ1,subQ0]});Q167=makeQuery(id+"F0.imprint","IMPRINT",FACE,{"disambiguationData":[TD([[makeQuery(id+"F0.imprint","IMPRINT",EDGE,{"disambiguationData":[TD([[subQ2,-1.0]])],"derivedFrom":subQ1}),1.0]])]});}
            var Q168;
            {var subQ0=sQuery(id+"F0.wireOp",EDGE,"E2");var subQ1=sQuery(id+"F0.wireOp",EDGE,"E0");var subQ2=makeQuery(id+"F0.imprint","INTERSECT",VERTEX,{"derivedFrom":[subQ1,subQ0]});Q168=makeQuery(id+"F0.imprint","IMPRINT",FACE,{"disambiguationData":[TD([[makeQuery(id+"F0.imprint","IMPRINT",EDGE,{"disambiguationData":[TD([[subQ2,-1.0]])],"derivedFrom":subQ1}),-1.0]])]});}
            var Q169;
            {var subQ0=sQuery(id+"F0.wireOp",EDGE,"E15");var subQ1=sQuery(id+"F0.wireOp",EDGE,"E0");var subQ2=makeQuery(id+"F0.imprint","INTERSECT",VERTEX,{"derivedFrom":[subQ1,subQ0]});Q169=makeQuery(id+"F0.imprint","IMPRINT",FACE,{"disambiguationData":[TD([[makeQuery(id+"F0.imprint","IMPRINT",EDGE,{"disambiguationData":[TD([[subQ2,-1.0]])],"derivedFrom":subQ1}),1.0]])]});}
            var Q170;
            {var subQ0=sQuery(id+"F0.wireOp",EDGE,"E5");var subQ1=sQuery(id+"F0.wireOp",EDGE,"E3");var subQ2=makeQuery(id+"F0.imprint","INTERSECT",VERTEX,{"derivedFrom":[subQ1,subQ0]});Q170=makeQuery(id+"F0.imprint","IMPRINT",FACE,{"disambiguationData":[TD([[makeQuery(id+"F0.imprint","IMPRINT",EDGE,{"disambiguationData":[TD([[subQ2,-1.0]])],"derivedFrom":subQ1}),-1.0]])]});}
            var Q171;
            {var subQ0=sQuery(id+"F0.wireOp",EDGE,"E10");var subQ1=sQuery(id+"F0.wireOp",EDGE,"E3");var subQ2=makeQuery(id+"F0.imprint","INTERSECT",VERTEX,{"derivedFrom":[subQ1,subQ0]});Q171=makeQuery(id+"F0.imprint","IMPRINT",FACE,{"disambiguationData":[TD([[makeQuery(id+"F0.imprint","IMPRINT",EDGE,{"disambiguationData":[TD([[subQ2,-1.0]])],"derivedFrom":subQ1}),-1.0]])]});}
            var Q172;
            {var subQ0=sQuery(id+"F0.wireOp",EDGE,"E15");var subQ1=sQuery(id+"F0.wireOp",EDGE,"E3");var subQ2=makeQuery(id+"F0.imprint","INTERSECT",VERTEX,{"derivedFrom":[subQ1,subQ0]});Q172=makeQuery(id+"F0.imprint","IMPRINT",FACE,{"disambiguationData":[TD([[makeQuery(id+"F0.imprint","IMPRINT",EDGE,{"disambiguationData":[TD([[subQ2,-1.0]])],"derivedFrom":subQ1}),1.0]])]});}
            var Q173;
            {var subQ0=sQuery(id+"F0.wireOp",EDGE,"E13");var subQ1=sQuery(id+"F0.wireOp",EDGE,"E3");var subQ2=makeQuery(id+"F0.imprint","INTERSECT",VERTEX,{"derivedFrom":[subQ1,subQ0]});Q173=makeQuery(id+"F0.imprint","IMPRINT",FACE,{"disambiguationData":[TD([[makeQuery(id+"F0.imprint","IMPRINT",EDGE,{"disambiguationData":[TD([[subQ2,-1.0]])],"derivedFrom":subQ1}),-1.0]])]});}
            var Q174;
            {var subQ0=sQuery(id+"F0.wireOp",EDGE,"E17");var subQ1=sQuery(id+"F0.wireOp",EDGE,"E8");var subQ2=makeQuery(id+"F0.imprint","INTERSECT",VERTEX,{"derivedFrom":[subQ1,subQ0]});Q174=makeQuery(id+"F0.imprint","IMPRINT",FACE,{"disambiguationData":[TD([[makeQuery(id+"F0.imprint","IMPRINT",EDGE,{"disambiguationData":[TD([[subQ2,-1.0]])],"derivedFrom":subQ1}),-1.0]])]});}
            var Q175;
            {var subQ0=sQuery(id+"F0.wireOp",EDGE,"E13");var subQ1=sQuery(id+"F0.wireOp",EDGE,"E1");var subQ2=makeQuery(id+"F0.imprint","INTERSECT",VERTEX,{"derivedFrom":[subQ1,subQ0]});Q175=makeQuery(id+"F0.imprint","IMPRINT",FACE,{"disambiguationData":[TD([[makeQuery(id+"F0.imprint","IMPRINT",EDGE,{"disambiguationData":[TD([[subQ2,-1.0]])],"derivedFrom":subQ1}),-1.0]])]});}
            var Q176;
            {var subQ0=sQuery(id+"F0.wireOp",EDGE,"E17");var subQ1=sQuery(id+"F0.wireOp",EDGE,"E1");var subQ2=makeQuery(id+"F0.imprint","INTERSECT",VERTEX,{"derivedFrom":[subQ1,subQ0]});Q176=makeQuery(id+"F0.imprint","IMPRINT",FACE,{"disambiguationData":[TD([[makeQuery(id+"F0.imprint","IMPRINT",EDGE,{"disambiguationData":[TD([[subQ2,-1.0]])],"derivedFrom":subQ1}),1.0]])]});}
            var Q177;
            {var subQ0=sQuery(id+"F0.wireOp",EDGE,"E6");var subQ1=sQuery(id+"F0.wireOp",EDGE,"E1");var subQ2=makeQuery(id+"F0.imprint","INTERSECT",VERTEX,{"derivedFrom":[subQ1,subQ0]});Q177=makeQuery(id+"F0.imprint","IMPRINT",FACE,{"disambiguationData":[TD([[makeQuery(id+"F0.imprint","IMPRINT",EDGE,{"disambiguationData":[TD([[subQ2,-1.0]])],"derivedFrom":subQ1}),1.0]])]});}
            var Q178;
            {var subQ0=sQuery(id+"F0.wireOp",EDGE,"E11");var subQ1=sQuery(id+"F0.wireOp",EDGE,"E1");var subQ2=makeQuery(id+"F0.imprint","INTERSECT",VERTEX,{"derivedFrom":[subQ1,subQ0]});Q178=makeQuery(id+"F0.imprint","IMPRINT",FACE,{"disambiguationData":[TD([[makeQuery(id+"F0.imprint","IMPRINT",EDGE,{"disambiguationData":[TD([[subQ2,-1.0]])],"derivedFrom":subQ1}),-1.0]])]});}
            var Q179;
            {var subQ0=sQuery(id+"F0.wireOp",EDGE,"E23");var subQ1=sQuery(id+"F0.wireOp",EDGE,"E1");var subQ2=makeQuery(id+"F0.imprint","INTERSECT",VERTEX,{"derivedFrom":[subQ1,subQ0]});Q179=makeQuery(id+"F0.imprint","IMPRINT",FACE,{"disambiguationData":[TD([[makeQuery(id+"F0.imprint","IMPRINT",EDGE,{"disambiguationData":[TD([[subQ2,-1.0]])],"derivedFrom":subQ1}),-1.0]])]});}
            var Q180;
            {var subQ0=sQuery(id+"F0.wireOp",EDGE,"E23");var subQ1=sQuery(id+"F0.wireOp",EDGE,"E6");var subQ2=makeQuery(id+"F0.imprint","INTERSECT",VERTEX,{"derivedFrom":[subQ1,subQ0]});Q180=makeQuery(id+"F0.imprint","IMPRINT",FACE,{"disambiguationData":[TD([[makeQuery(id+"F0.imprint","IMPRINT",EDGE,{"disambiguationData":[TD([[subQ2,-1.0]])],"derivedFrom":subQ1}),-1.0]])]});}
            var Q181;
            {var subQ0=sQuery(id+"F0.wireOp",EDGE,"E11");var subQ1=sQuery(id+"F0.wireOp",EDGE,"E4");var subQ2=makeQuery(id+"F0.imprint","INTERSECT",VERTEX,{"derivedFrom":[subQ1,subQ0]});Q181=makeQuery(id+"F0.imprint","IMPRINT",FACE,{"disambiguationData":[TD([[makeQuery(id+"F0.imprint","IMPRINT",EDGE,{"disambiguationData":[TD([[subQ2,-1.0]])],"derivedFrom":subQ1}),-1.0]])]});}
            var Q182;
            {var subQ0=sQuery(id+"F0.wireOp",EDGE,"E23");var subQ1=sQuery(id+"F0.wireOp",EDGE,"E4");var subQ2=makeQuery(id+"F0.imprint","INTERSECT",VERTEX,{"derivedFrom":[subQ1,subQ0]});Q182=makeQuery(id+"F0.imprint","IMPRINT",FACE,{"disambiguationData":[TD([[makeQuery(id+"F0.imprint","IMPRINT",EDGE,{"disambiguationData":[TD([[subQ2,-1.0]])],"derivedFrom":subQ1}),1.0]])]});}
            var Q183;
            {var subQ0=sQuery(id+"F0.wireOp",EDGE,"E9");var subQ1=sQuery(id+"F0.wireOp",EDGE,"E4");var subQ2=makeQuery(id+"F0.imprint","INTERSECT",VERTEX,{"derivedFrom":[subQ1,subQ0]});Q183=makeQuery(id+"F0.imprint","IMPRINT",FACE,{"disambiguationData":[TD([[makeQuery(id+"F0.imprint","IMPRINT",EDGE,{"disambiguationData":[TD([[subQ2,-1.0]])],"derivedFrom":subQ1}),1.0]])]});}
            var Q184;
            {var subQ0=sQuery(id+"F0.wireOp",EDGE,"E18");var subQ1=sQuery(id+"F0.wireOp",EDGE,"E9");var subQ2=makeQuery(id+"F0.imprint","INTERSECT",VERTEX,{"derivedFrom":[subQ1,subQ0]});Q184=makeQuery(id+"F0.imprint","IMPRINT",FACE,{"disambiguationData":[TD([[makeQuery(id+"F0.imprint","IMPRINT",EDGE,{"disambiguationData":[TD([[subQ2,-1.0]])],"derivedFrom":subQ1}),-1.0]])]});}
            var Q185;
            {var subQ0=sQuery(id+"F0.wireOp",EDGE,"E14");var subQ1=sQuery(id+"F0.wireOp",EDGE,"E2");var subQ2=makeQuery(id+"F0.imprint","INTERSECT",VERTEX,{"derivedFrom":[subQ1,subQ0]});Q185=makeQuery(id+"F0.imprint","IMPRINT",FACE,{"disambiguationData":[TD([[makeQuery(id+"F0.imprint","IMPRINT",EDGE,{"disambiguationData":[TD([[subQ2,-1.0]])],"derivedFrom":subQ1}),-1.0]])]});}
            var Q186;
            {var subQ0=sQuery(id+"F0.wireOp",EDGE,"E18");var subQ1=sQuery(id+"F0.wireOp",EDGE,"E7");var subQ2=makeQuery(id+"F0.imprint","INTERSECT",VERTEX,{"derivedFrom":[subQ1,subQ0]});Q186=makeQuery(id+"F0.imprint","IMPRINT",FACE,{"disambiguationData":[TD([[makeQuery(id+"F0.imprint","IMPRINT",EDGE,{"disambiguationData":[TD([[subQ2,-1.0]])],"derivedFrom":subQ1}),1.0]])]});}
            var Q187;
            {var subQ0=sQuery(id+"F0.wireOp",EDGE,"E18");var subQ1=sQuery(id+"F0.wireOp",EDGE,"E2");var subQ2=makeQuery(id+"F0.imprint","INTERSECT",VERTEX,{"derivedFrom":[subQ1,subQ0]});Q187=makeQuery(id+"F0.imprint","IMPRINT",FACE,{"disambiguationData":[TD([[makeQuery(id+"F0.imprint","IMPRINT",EDGE,{"disambiguationData":[TD([[subQ2,-1.0]])],"derivedFrom":subQ1}),1.0]])]});}
            var Q188;
            {var subQ0=sQuery(id+"F0.wireOp",EDGE,"E7");var subQ1=sQuery(id+"F0.wireOp",EDGE,"E2");var subQ2=makeQuery(id+"F0.imprint","INTERSECT",VERTEX,{"derivedFrom":[subQ1,subQ0]});Q188=makeQuery(id+"F0.imprint","IMPRINT",FACE,{"disambiguationData":[TD([[makeQuery(id+"F0.imprint","IMPRINT",EDGE,{"disambiguationData":[TD([[subQ2,-1.0]])],"derivedFrom":subQ1}),1.0]])]});}
            var Q189;
            {var subQ0=sQuery(id+"F0.wireOp",EDGE,"E16");var subQ1=sQuery(id+"F0.wireOp",EDGE,"E7");var subQ2=makeQuery(id+"F0.imprint","INTERSECT",VERTEX,{"derivedFrom":[subQ1,subQ0]});Q189=makeQuery(id+"F0.imprint","IMPRINT",FACE,{"disambiguationData":[TD([[makeQuery(id+"F0.imprint","IMPRINT",EDGE,{"disambiguationData":[TD([[subQ2,-1.0]])],"derivedFrom":subQ1}),-1.0]])]});}
            var Q190;
            {var subQ0=sQuery(id+"F0.wireOp",EDGE,"E7");var subQ1=sQuery(id+"F0.wireOp",EDGE,"E0");var subQ2=makeQuery(id+"F0.imprint","INTERSECT",VERTEX,{"derivedFrom":[subQ1,subQ0]});Q190=makeQuery(id+"F0.imprint","IMPRINT",FACE,{"disambiguationData":[TD([[makeQuery(id+"F0.imprint","IMPRINT",EDGE,{"disambiguationData":[TD([[subQ2,-1.0]])],"derivedFrom":subQ1}),-1.0]])]});}
            var Q191;
            {var subQ0=sQuery(id+"F0.wireOp",EDGE,"E12");var subQ1=sQuery(id+"F0.wireOp",EDGE,"E0");var subQ2=makeQuery(id+"F0.imprint","INTERSECT",VERTEX,{"derivedFrom":[subQ1,subQ0]});Q191=makeQuery(id+"F0.imprint","IMPRINT",FACE,{"disambiguationData":[TD([[makeQuery(id+"F0.imprint","IMPRINT",EDGE,{"disambiguationData":[TD([[subQ2,-1.0]])],"derivedFrom":subQ1}),-1.0]])]});}
            var Q192;
            {var subQ0=sQuery(id+"F0.wireOp",EDGE,"E12");var subQ1=sQuery(id+"F0.wireOp",EDGE,"E0");var subQ2=makeQuery(id+"F0.imprint","INTERSECT",VERTEX,{"derivedFrom":[subQ1,subQ0]});Q192=makeQuery(id+"F0.imprint","IMPRINT",FACE,{"disambiguationData":[TD([[makeQuery(id+"F0.imprint","IMPRINT",EDGE,{"disambiguationData":[TD([[subQ2,-1.0]])],"derivedFrom":subQ1}),1.0]])]});}
            var Q193;
            {var subQ0=sQuery(id+"F0.wireOp",EDGE,"E16");var subQ1=sQuery(id+"F0.wireOp",EDGE,"E5");var subQ2=makeQuery(id+"F0.imprint","INTERSECT",VERTEX,{"derivedFrom":[subQ1,subQ0]});Q193=makeQuery(id+"F0.imprint","IMPRINT",FACE,{"disambiguationData":[TD([[makeQuery(id+"F0.imprint","IMPRINT",EDGE,{"disambiguationData":[TD([[subQ2,-1.0]])],"derivedFrom":subQ1}),1.0]])]});}
            var Q194;
            {var subQ0=sQuery(id+"F0.wireOp",EDGE,"E10");var subQ1=sQuery(id+"F0.wireOp",EDGE,"E0");var subQ2=makeQuery(id+"F0.imprint","INTERSECT",VERTEX,{"derivedFrom":[subQ1,subQ0]});Q194=makeQuery(id+"F0.imprint","IMPRINT",FACE,{"disambiguationData":[TD([[makeQuery(id+"F0.imprint","IMPRINT",EDGE,{"disambiguationData":[TD([[subQ2,-1.0]])],"derivedFrom":subQ1}),1.0]])]});}
            var Q195;
            {var subQ0=sQuery(id+"F0.wireOp",EDGE,"E15");var subQ1=sQuery(id+"F0.wireOp",EDGE,"E0");var subQ2=makeQuery(id+"F0.imprint","INTERSECT",VERTEX,{"derivedFrom":[subQ1,subQ0]});Q195=makeQuery(id+"F0.imprint","IMPRINT",FACE,{"disambiguationData":[TD([[makeQuery(id+"F0.imprint","IMPRINT",EDGE,{"disambiguationData":[TD([[subQ2,-1.0]])],"derivedFrom":subQ1}),-1.0]])]});}
            var Q196;
            {var subQ0=sQuery(id+"F0.wireOp",EDGE,"E16");var subQ1=sQuery(id+"F0.wireOp",EDGE,"E0");var subQ2=makeQuery(id+"F0.imprint","INTERSECT",VERTEX,{"derivedFrom":[subQ1,subQ0]});Q196=makeQuery(id+"F0.imprint","IMPRINT",FACE,{"disambiguationData":[TD([[makeQuery(id+"F0.imprint","IMPRINT",EDGE,{"disambiguationData":[TD([[subQ2,-1.0]])],"derivedFrom":subQ1}),1.0]])]});}
            var Q197;
            {var subQ0=sQuery(id+"F0.wireOp",EDGE,"E5");var subQ1=sQuery(id+"F0.wireOp",EDGE,"E0");var subQ2=makeQuery(id+"F0.imprint","INTERSECT",VERTEX,{"derivedFrom":[subQ1,subQ0]});Q197=makeQuery(id+"F0.imprint","IMPRINT",FACE,{"disambiguationData":[TD([[makeQuery(id+"F0.imprint","IMPRINT",EDGE,{"disambiguationData":[TD([[subQ2,-1.0]])],"derivedFrom":subQ1}),1.0]])]});}
            var Q198;
            {var subQ0=sQuery(id+"F0.wireOp",EDGE,"E10");var subQ1=sQuery(id+"F0.wireOp",EDGE,"E0");var subQ2=makeQuery(id+"F0.imprint","INTERSECT",VERTEX,{"derivedFrom":[subQ1,subQ0]});Q198=makeQuery(id+"F0.imprint","IMPRINT",FACE,{"disambiguationData":[TD([[makeQuery(id+"F0.imprint","IMPRINT",EDGE,{"disambiguationData":[TD([[subQ2,-1.0]])],"derivedFrom":subQ1}),-1.0]])]});}
            var Q199;
            {var subQ0=sQuery(id+"F0.wireOp",EDGE,"E15");var subQ1=sQuery(id+"F0.wireOp",EDGE,"E5");var subQ2=makeQuery(id+"F0.imprint","INTERSECT",VERTEX,{"derivedFrom":[subQ1,subQ0]});Q199=makeQuery(id+"F0.imprint","IMPRINT",FACE,{"disambiguationData":[TD([[makeQuery(id+"F0.imprint","IMPRINT",EDGE,{"disambiguationData":[TD([[subQ2,-1.0]])],"derivedFrom":subQ1}),-1.0]])]});}
            extrude(context, id + "F1", {"entities" : qUnion([Q0, Q1, Q2, Q3, Q4, Q5, Q6, Q7, Q8, Q9, Q10, Q11, Q12, Q13, Q14, Q15, Q16, Q17, Q18, Q19, Q20, Q21, Q22, Q23, Q24, Q25, Q26, Q27, Q28, Q29, Q30, Q31, Q32, Q33, Q34, Q35, Q36, Q37, Q38, Q39, Q40, Q41, Q42, Q43, Q44, Q45, Q46, Q47, Q48, Q49, Q50, Q51, Q52, Q53, Q54, Q55, Q56, Q57, Q58, Q59, Q60, Q61, Q62, Q63, Q64, Q65, Q66, Q67, Q68, Q69, Q70, Q71, Q72, Q73, Q74, Q75, Q76, Q77, Q78, Q79, Q80, Q81, Q82, Q83, Q84, Q85, Q86, Q87, Q88, Q89, Q90, Q91, Q92, Q93, Q94, Q95, Q96, Q97, Q98, Q99, Q100, Q101, Q102, Q103, Q104, Q105, Q106, Q107, Q108, Q109, Q110, Q111, Q112, Q113, Q114, Q115, Q116, Q117, Q118, Q119, Q120, Q121, Q122, Q123, Q124, Q125, Q126, Q127, Q128, Q129, Q130, Q131, Q132, Q133, Q134, Q135, Q136, Q137, Q138, Q139, Q140, Q141, Q142, Q143, Q144, Q145, Q146, Q147, Q148, Q149, Q150, Q151, Q152, Q153, Q154, Q155, Q156, Q157, Q158, Q159, Q160, Q161, Q162, Q163, Q164, Q165, Q166, Q167, Q168, Q169, Q170, Q171, Q172, Q173, Q174, Q175, Q176, Q177, Q178, Q179, Q180, Q181, Q182, Q183, Q184, Q185, Q186, Q187, Q188, Q189, Q190, Q191, Q192, Q193, Q194, Q195, Q196, Q197, Q198, Q199]), "depth" : 6.35 * mm});
        }
    });
